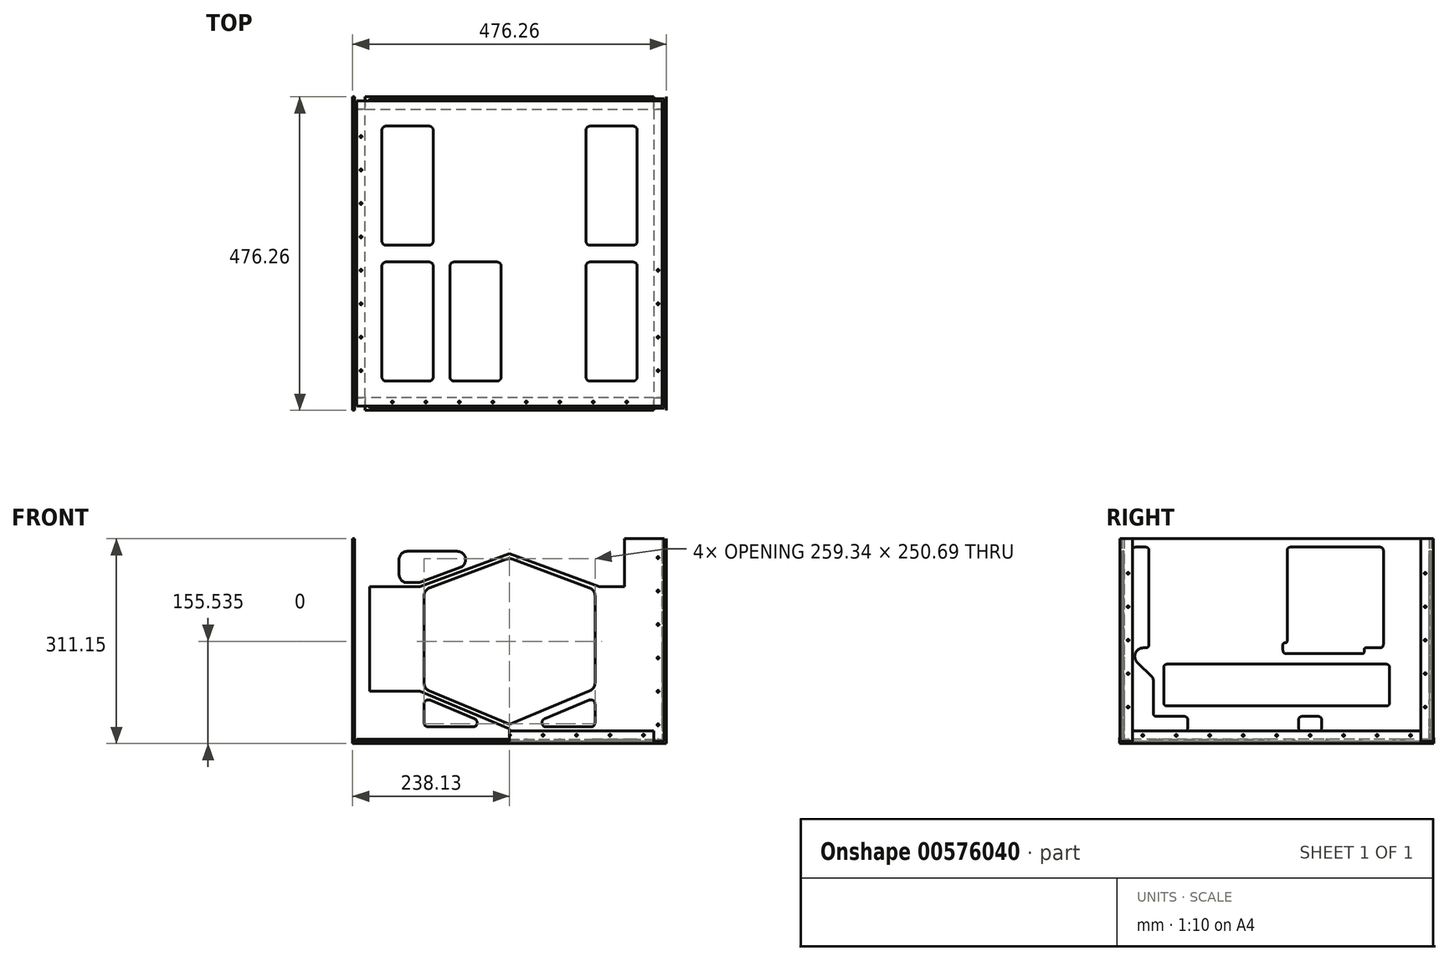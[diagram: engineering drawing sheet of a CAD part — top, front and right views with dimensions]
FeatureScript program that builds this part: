
annotation { "Feature Type Name" : "Feature", "Feature Type Description" : "" }
export const myFeature = defineFeature(function(context is Context, id is Id, definition is map)
    precondition{}
    {
        {
            var Q0;
            Q0=qCreatedBy(makeId("Top.planeOp"),FACE);
            var sketch = newSketch(context, id + "F0", { "sketchPlane" : qUnion([Q0])});
            skLineSegment(sketch, "E0.bottom", {"start": v(231.77, -231.77) * mm, "end": v(-231.78, -231.78) * mm});
            skLineSegment(sketch, "E0.top", {"start": v(231.77, 231.78) * mm, "end": v(-231.78, 231.77) * mm});
            skLineSegment(sketch, "E0.left", {"start": v(231.77, -231.77) * mm, "end": v(231.77, 231.78) * mm});
            skLineSegment(sketch, "E0.right", {"start": v(-231.78, -231.78) * mm, "end": v(-231.78, 231.77) * mm});
            skPoint(sketch, "E0.middle", {"position": v(0, 0) * mm});
            skLineSegment(sketch, "E1.0", {"start": v(234.95, -234.95) * mm, "end": v(234.95, 234.95) * mm});
            skLineSegment(sketch, "E1.1", {"start": v(234.95, -234.95) * mm, "end": v(-234.95, -234.95) * mm});
            skLineSegment(sketch, "E1.2", {"start": v(-234.95, -234.95) * mm, "end": v(-234.95, 234.95) * mm});
            skLineSegment(sketch, "E1.3", {"start": v(234.95, 234.95) * mm, "end": v(-234.95, 234.95) * mm});
            skLineSegment(sketch, "E2", {"start": v(-231.78, 231.77) * mm, "end": v(-234.95, 231.77) * mm});
            skLineSegment(sketch, "E3.MirrorCS", {"start": v(231.78, 231.77) * mm, "end": v(234.95, 231.77) * mm});
            skLineSegment(sketch, "E4.MirrorCS", {"start": v(-231.78, -231.77) * mm, "end": v(-234.95, -231.77) * mm});
            skLineSegment(sketch, "E5.MirrorCS", {"start": v(231.78, -231.77) * mm, "end": v(234.95, -231.77) * mm});
            skLineSegment(sketch, "E6.0", {"start": v(238.12, 238.13) * mm, "end": v(-238.13, 238.12) * mm});
            skLineSegment(sketch, "E6.1", {"start": v(238.12, -238.12) * mm, "end": v(238.12, 238.13) * mm});
            skLineSegment(sketch, "E6.2", {"start": v(238.12, -238.12) * mm, "end": v(-238.13, -238.13) * mm});
            skLineSegment(sketch, "E6.3", {"start": v(-238.13, -238.13) * mm, "end": v(-238.13, 238.12) * mm});
            skLineSegment(sketch, "E7", {"start": v(-238.13, 238.12) * mm, "end": v(-219.08, 238.12) * mm});
            skLineSegment(sketch, "E8", {"start": v(-219.08, 238.12) * mm, "end": v(-219.08, 234.95) * mm});
            skLineSegment(sketch, "E9", {"start": v(-238.13, 238.12) * mm, "end": v(-238.13, 219.07) * mm});
            skLineSegment(sketch, "E10", {"start": v(-238.13, 219.07) * mm, "end": v(-234.95, 219.07) * mm});
            skLineSegment(sketch, "E11.MirrorCS", {"start": v(238.13, 219.07) * mm, "end": v(234.95, 219.07) * mm});
            skLineSegment(sketch, "E12.MirrorCS", {"start": v(219.08, 238.12) * mm, "end": v(219.08, 234.95) * mm});
            skLineSegment(sketch, "E13.MirrorCS", {"start": v(238.13, 238.12) * mm, "end": v(219.08, 238.12) * mm});
            skLineSegment(sketch, "E14.MirrorCS", {"start": v(238.13, 238.12) * mm, "end": v(238.13, 219.07) * mm});
            skLineSegment(sketch, "E15.MirrorCS", {"start": v(-238.13, -219.07) * mm, "end": v(-234.95, -219.07) * mm});
            skLineSegment(sketch, "E16.MirrorCS", {"start": v(-219.08, -238.12) * mm, "end": v(-219.08, -234.95) * mm});
            skLineSegment(sketch, "E17.MirrorCS", {"start": v(-238.13, -238.12) * mm, "end": v(-238.13, -219.07) * mm});
            skLineSegment(sketch, "E18.MirrorCS", {"start": v(-238.13, -238.12) * mm, "end": v(-219.08, -238.12) * mm});
            skLineSegment(sketch, "E19.MirrorCS", {"start": v(238.13, -219.07) * mm, "end": v(234.95, -219.07) * mm});
            skLineSegment(sketch, "E20.MirrorCS", {"start": v(219.08, -238.12) * mm, "end": v(219.08, -234.95) * mm});
            skLineSegment(sketch, "E21.MirrorCS", {"start": v(238.13, -238.12) * mm, "end": v(219.08, -238.12) * mm});
            skLineSegment(sketch, "E22.MirrorCS", {"start": v(238.13, -238.12) * mm, "end": v(238.13, -219.07) * mm});
            skSolve(sketch);
        }
        {
            var Q0;
            Q0=makeQuery(id+"F0.imprint","IMPRINT",FACE,{"disambiguationData":[TD([[makeQuery(id+"F0.imprint","IMPRINT",EDGE,{"derivedFrom":sQuery(id+"F0.wireOp",EDGE,"E0.left")}),-1.0]])]});
            var Q1;
            Q1=makeQuery(id+"F0.imprint","IMPRINT",FACE,{"disambiguationData":[TD([[makeQuery(id+"F0.imprint","IMPRINT",EDGE,{"derivedFrom":sQuery(id+"F0.wireOp",EDGE,"E0.right")}),1.0]])]});
            extrude(context, id + "F1", {"entities" : qUnion([Q0, Q1]), "depth" : 307.97 * mm, "offsetDistance" : 25.4 * mm});
        }
        {
            var Q0;
            Q0=makeQuery(id+"F0.imprint","IMPRINT",FACE,{"disambiguationData":[TD([[makeQuery(id+"F0.imprint","IMPRINT",EDGE,{"derivedFrom":sQuery(id+"F0.wireOp",EDGE,"E0.top")}),-1.0]])]});
            var Q1;
            Q1=makeQuery(id+"F0.imprint","IMPRINT",FACE,{"disambiguationData":[TD([[makeQuery(id+"F0.imprint","IMPRINT",EDGE,{"derivedFrom":sQuery(id+"F0.wireOp",EDGE,"E0.bottom")}),1.0]])]});
            extrude(context, id + "F2", {"entities" : qUnion([Q0, Q1]), "depth" : 307.97 * mm, "offsetDistance" : 25.4 * mm});
        }
        {
            var Q0;
            {var subQ0=sQuery(id+"F0.wireOp",EDGE,"E15.MirrorCS");Q0=makeQuery(id+"F0.imprint","IMPRINT",FACE,{"disambiguationData":[TD([[makeQuery(id+"F0.imprint","IMPRINT",EDGE,{"derivedFrom":subQ0}),-1.0]])]});}
            var Q1;
            {var subQ0=sQuery(id+"F0.wireOp",EDGE,"E19.MirrorCS");Q1=makeQuery(id+"F0.imprint","IMPRINT",FACE,{"disambiguationData":[TD([[makeQuery(id+"F0.imprint","IMPRINT",EDGE,{"derivedFrom":subQ0}),1.0]])]});}
            var Q2;
            {var subQ0=sQuery(id+"F0.wireOp",EDGE,"E11.MirrorCS");Q2=makeQuery(id+"F0.imprint","IMPRINT",FACE,{"disambiguationData":[TD([[makeQuery(id+"F0.imprint","IMPRINT",EDGE,{"derivedFrom":subQ0}),-1.0]])]});}
            var Q3;
            Q3=makeQuery(id+"F0.imprint","IMPRINT",FACE,{"disambiguationData":[TD([[makeQuery(id+"F0.imprint","IMPRINT",EDGE,{"derivedFrom":sQuery(id+"F0.wireOp",EDGE,"E7")}),-1.0]])]});
            extrude(context, id + "F3", {"entities" : qUnion([Q0, Q1, Q2, Q3]), "depth" : 307.97 * mm, "offsetDistance" : 25.4 * mm});
        }
        {
            var Q0;
            Q0=makeQuery(id+"F3.opExtrude","SWEPT_FACE",FACE,{"disambiguationData":[OSD([sQuery(id+"F0.wireOp",EDGE,"E16.MirrorCS")])]});
            var sketch = newSketch(context, id + "F4", { "sketchPlane" : qUnion([Q0])});
            skLineSegment(sketch, "E23", {"start": v(-234.95, 0) * mm, "end": v(-234.95, -3.18) * mm});
            skLineSegment(sketch, "E24", {"start": v(-234.95, -3.18) * mm, "end": v(-238.13, -3.18) * mm});
            skLineSegment(sketch, "E25", {"start": v(-238.13, -3.18) * mm, "end": v(-238.12, 15.88) * mm});
            skLineSegment(sketch, "E26", {"start": v(-238.12, 15.88) * mm, "end": v(-234.95, 15.88) * mm});
            skLineSegment(sketch, "E27", {"start": v(-234.95, 15.88) * mm, "end": v(-234.95, 0) * mm});
            skLineSegment(sketch, "E28", {"start": v(-238.13, -3.18) * mm, "end": v(-219.08, -3.18) * mm});
            skLineSegment(sketch, "E29", {"start": v(-219.08, -3.18) * mm, "end": v(-219.08, 0) * mm});
            skLineSegment(sketch, "E30", {"start": v(-219.08, 0) * mm, "end": v(-234.95, 0) * mm});
            skSolve(sketch);
        }
        {
            var Q0;
            Q0=qSketchRegion(id+"F4",true);
            extrude(context, id + "F5", {"entities" : qUnion([Q0]), "depth" : 438.15 * mm, "offsetDistance" : 25.4 * mm});
        }
        {
            var Q0;
            Q0=qCreatedBy(makeId("Front.planeOp"),FACE);
            var sketch = newSketch(context, id + "F6", { "sketchPlane" : qUnion([Q0])});
            skLineSegment(sketch, "E31", {"start": v(0, 0) * mm, "end": v(0, 52.73) * mm});
            skSolve(sketch);
        }
        {
            var Q0;
            Q0=makeQuery(id+"F5.opExtrude","SWEPT_BODY",BODY,{"disambiguationData":[OSD([sQuery(id+"F4.wireOp",EDGE,"E25"),sQuery(id+"F4.wireOp",EDGE,"E26"),sQuery(id+"F4.wireOp",EDGE,"E27"),sQuery(id+"F4.wireOp",EDGE,"E28"),sQuery(id+"F4.wireOp",EDGE,"E29"),sQuery(id+"F4.wireOp",EDGE,"E30")])]});
            var Q1;
            Q1=sQuery(id+"F6.wireOp",EDGE,"E31");
            circularPattern(context, id + "F7", {"entities" : qUnion([Q0]), "axis" : qUnion([Q1]), "angle" : 360 * degree, "instanceCount" : 4, "equalSpace" : true});
        }
        {
            var Q0;
            Q0=makeQuery(id+"F2.opExtrude","SWEPT_FACE",FACE,{"disambiguationData":[OSD([sQuery(id+"F0.wireOp",EDGE,"E1.1")])]});
            var sketch = newSketch(context, id + "F8", { "sketchPlane" : qUnion([Q0])});
            skLineSegment(sketch, "E32.bottom", {"start": v(212.22, 76.2) * mm, "end": v(136.02, 76.2) * mm});
            skLineSegment(sketch, "E32.top", {"start": v(212.22, 234.95) * mm, "end": v(136.02, 234.95) * mm});
            skLineSegment(sketch, "E32.left", {"start": v(212.22, 76.2) * mm, "end": v(212.22, 234.95) * mm});
            skLineSegment(sketch, "E32.right", {"start": v(136.02, 76.2) * mm, "end": v(136.02, 234.95) * mm});
            skPoint(sketch, "E32.middle", {"position": v(174.12, 155.58) * mm});
            skLineSegment(sketch, "E33", {"start": v(219.08, 307.98) * mm, "end": v(174.12, 307.98) * mm});
            skLineSegment(sketch, "E34", {"start": v(174.12, 307.98) * mm, "end": v(174.12, 155.58) * mm});
            skLineSegment(sketch, "E35", {"start": v(0, 307.98) * mm, "end": v(0, 348.73) * mm});
            skPoint(sketch, "E35.endSnap0", {"position": v(0, 307.98) * mm});
            skLineSegment(sketch, "E36", {"start": v(219.08, 307.98) * mm, "end": v(219.08, 288.93) * mm});
            skLineSegment(sketch, "E37", {"start": v(206.38, 288.93) * mm, "end": v(193.17, 288.93) * mm});
            skLineSegment(sketch, "E38", {"start": v(136.02, 234.95) * mm, "end": v(-2.34, 286.18) * mm});
            skLineSegment(sketch, "E39", {"start": v(136.02, 76.2) * mm, "end": v(0, 19.05) * mm});
            skLineSegment(sketch, "E40.0", {"start": v(135.02, 242.1) * mm, "end": v(75, 264.32) * mm});
            skLineSegment(sketch, "E41.0", {"start": v(121.38, 233.6) * mm, "end": v(4.4, 276.9) * mm});
            skLineSegment(sketch, "E42.0", {"start": v(121.89, 77.15) * mm, "end": v(4.92, 28) * mm});
            skLineSegment(sketch, "E43.0", {"start": v(167.77, 276.23) * mm, "end": v(167.77, 254) * mm});
            skLineSegment(sketch, "E44.0", {"start": v(180.47, 276.23) * mm, "end": v(180.47, 254) * mm});
            skLineSegment(sketch, "E45", {"start": v(212.22, 234.95) * mm, "end": v(219.07, 234.95) * mm});
            skLineSegment(sketch, "E46", {"start": v(212.22, 76.2) * mm, "end": v(219.07, 76.2) * mm});
            skLineSegment(sketch, "E47.1", {"start": v(212.22, 241.3) * mm, "end": v(219.07, 241.3) * mm});
            skLineSegment(sketch, "E47.2", {"start": v(155.07, 241.3) * mm, "end": v(139.43, 241.3) * mm});
            skLineSegment(sketch, "E47.3", {"start": v(129.67, 88.86) * mm, "end": v(129.67, 221.69) * mm});
            skLineSegment(sketch, "E48", {"start": v(0, -253.23) * mm, "end": v(0, 278.54) * mm});
            skArc(sketch, "E49.filletArc", {"start": v(129.67, 221.69) * mm, "mid": v(127.4, 228.95) * mm, "end": v(121.38, 233.6) * mm});
            skArc(sketch, "E50.filletArc", {"start": v(121.89, 77.15) * mm, "mid": v(127.54, 81.83) * mm, "end": v(129.67, 88.86) * mm});
            skArc(sketch, "E51.filletArc", {"start": v(135.02, 242.1) * mm, "mid": v(137.2, 241.5) * mm, "end": v(139.43, 241.3) * mm});
            skArc(sketch, "E52.filletArc", {"start": v(155.07, 241.3) * mm, "mid": v(164.05, 245.02) * mm, "end": v(167.77, 254) * mm});
            skLineSegment(sketch, "E53", {"start": v(206.37, 241.3) * mm, "end": v(193.17, 241.3) * mm});
            skArc(sketch, "E54.filletArc", {"start": v(180.47, 254) * mm, "mid": v(184.19, 245.02) * mm, "end": v(193.17, 241.3) * mm});
            skLineSegment(sketch, "E55", {"start": v(219.08, 276.23) * mm, "end": v(219.08, 254) * mm});
            skPoint(sketch, "E56.visualSharp", {"position": v(219.07, 241.3) * mm});
            skArc(sketch, "E56.filletArc", {"start": v(206.37, 241.3) * mm, "mid": v(215.36, 245.02) * mm, "end": v(219.07, 254) * mm});
            skPoint(sketch, "E57.visualSharp", {"position": v(219.08, 288.93) * mm});
            skArc(sketch, "E57.filletArc", {"start": v(219.08, 276.23) * mm, "mid": v(215.36, 285.2) * mm, "end": v(206.38, 288.93) * mm});
            skPoint(sketch, "E58.newPointB", {"position": v(0, 288.93) * mm});
            skArc(sketch, "E58.filletArc", {"start": v(193.17, 288.93) * mm, "mid": v(184.19, 285.2) * mm, "end": v(180.47, 276.23) * mm});
            skPoint(sketch, "E59.visualSharp", {"position": v(219.08, 15.88) * mm});
            skPoint(sketch, "E60.newPointB", {"position": v(0, 15.87) * mm});
            skLineSegment(sketch, "E61", {"start": v(155.07, 288.93) * mm, "end": v(79.4, 288.93) * mm});
            skArc(sketch, "E62.filletArc", {"start": v(167.77, 276.23) * mm, "mid": v(164.05, 285.2) * mm, "end": v(155.07, 288.93) * mm});
            skPoint(sketch, "E63.visualSharp", {"position": v(8.53, 288.93) * mm});
            skArc(sketch, "E63.filletArc", {"start": v(79.4, 288.93) * mm, "mid": v(66.9, 278.46) * mm, "end": v(75, 264.32) * mm});
            skPoint(sketch, "E64.visualSharp", {"position": v(8.76, 15.88) * mm});
            skPoint(sketch, "E65.visualSharp", {"position": v(167.77, 15.88) * mm});
            skArc(sketch, "E66.MirrorCS", {"start": v(-135.02, 242.1) * mm, "mid": v(-137.2, 241.5) * mm, "end": v(-139.43, 241.3) * mm});
            skLineSegment(sketch, "E67.MirrorCS", {"start": v(-212.22, 241.3) * mm, "end": v(-219.07, 241.3) * mm});
            skLineSegment(sketch, "E68.MirrorCS", {"start": v(-212.22, 234.95) * mm, "end": v(-219.07, 234.95) * mm});
            skLineSegment(sketch, "E69.MirrorCS", {"start": v(-136.02, 76.2) * mm, "end": v(0, 19.05) * mm});
            skArc(sketch, "E70.MirrorCS", {"start": v(-167.77, 276.23) * mm, "mid": v(-164.05, 285.2) * mm, "end": v(-155.07, 288.93) * mm});
            skLineSegment(sketch, "E71.MirrorCS", {"start": v(-136.02, 234.95) * mm, "end": v(2.34, 286.18) * mm});
            skArc(sketch, "E72.MirrorCS", {"start": v(-219.07, 276.23) * mm, "mid": v(-215.36, 285.2) * mm, "end": v(-206.37, 288.93) * mm});
            skLineSegment(sketch, "E73.MirrorCS", {"start": v(-219.07, 307.98) * mm, "end": v(-219.07, 288.93) * mm});
            skLineSegment(sketch, "E74.MirrorCS", {"start": v(-129.67, 88.86) * mm, "end": v(-129.67, 221.69) * mm});
            skLineSegment(sketch, "E75.MirrorCS", {"start": v(-206.37, 288.92) * mm, "end": v(-193.17, 288.92) * mm});
            skLineSegment(sketch, "E76.MirrorCS", {"start": v(-174.12, 307.98) * mm, "end": v(-174.12, 155.57) * mm});
            skLineSegment(sketch, "E77.MirrorCS", {"start": v(-121.89, 77.15) * mm, "end": v(-4.92, 28) * mm});
            skPoint(sketch, "E78.MirrorP", {"position": v(-219.07, 288.93) * mm});
            skPoint(sketch, "E79.MirrorP", {"position": v(-174.12, 155.57) * mm});
            skPoint(sketch, "E80.MirrorP", {"position": v(-8.53, 288.93) * mm});
            skLineSegment(sketch, "E81.MirrorCS", {"start": v(-136.02, 76.2) * mm, "end": v(-136.02, 234.95) * mm});
            skLineSegment(sketch, "E82.MirrorCS", {"start": v(-212.22, 76.2) * mm, "end": v(-212.22, 234.95) * mm});
            skLineSegment(sketch, "E83.MirrorCS", {"start": v(-219.07, 307.98) * mm, "end": v(-174.12, 307.98) * mm});
            skLineSegment(sketch, "E84.MirrorCS", {"start": v(-212.22, 234.95) * mm, "end": v(-136.02, 234.95) * mm});
            skLineSegment(sketch, "E85.MirrorCS", {"start": v(-155.07, 241.3) * mm, "end": v(-139.43, 241.3) * mm});
            skArc(sketch, "E86.MirrorCS", {"start": v(-79.4, 288.93) * mm, "mid": v(-66.9, 278.46) * mm, "end": v(-75, 264.32) * mm});
            skPoint(sketch, "E87.MirrorP", {"position": v(-219.07, 241.3) * mm});
            skLineSegment(sketch, "E88.MirrorCS", {"start": v(-206.37, 241.3) * mm, "end": v(-193.17, 241.3) * mm});
            skPoint(sketch, "E89.MirrorP", {"position": v(-8.76, 15.88) * mm});
            skLineSegment(sketch, "E90.MirrorCS", {"start": v(-155.07, 288.93) * mm, "end": v(-79.4, 288.93) * mm});
            skArc(sketch, "E91.MirrorCS", {"start": v(-193.17, 288.93) * mm, "mid": v(-184.19, 285.2) * mm, "end": v(-180.47, 276.23) * mm});
            skLineSegment(sketch, "E92.MirrorCS", {"start": v(-180.47, 276.23) * mm, "end": v(-180.47, 254) * mm});
            skLineSegment(sketch, "E93.MirrorCS", {"start": v(-219.07, 276.23) * mm, "end": v(-219.07, 254) * mm});
            skArc(sketch, "E94.MirrorCS", {"start": v(-121.89, 77.15) * mm, "mid": v(-127.54, 81.83) * mm, "end": v(-129.67, 88.86) * mm});
            skLineSegment(sketch, "E95.MirrorCS", {"start": v(-167.77, 276.23) * mm, "end": v(-167.77, 254) * mm});
            skArc(sketch, "E96.MirrorCS", {"start": v(-206.37, 241.3) * mm, "mid": v(-215.36, 245.02) * mm, "end": v(-219.07, 254) * mm});
            skLineSegment(sketch, "E97.MirrorCS", {"start": v(-135.02, 242.1) * mm, "end": v(-75, 264.32) * mm});
            skArc(sketch, "E98.MirrorCS", {"start": v(-129.67, 221.69) * mm, "mid": v(-127.4, 228.95) * mm, "end": v(-121.38, 233.6) * mm});
            skArc(sketch, "E99.MirrorCS", {"start": v(-155.07, 241.3) * mm, "mid": v(-164.05, 245.02) * mm, "end": v(-167.77, 254) * mm});
            skArc(sketch, "E100.MirrorCS", {"start": v(-180.47, 254) * mm, "mid": v(-184.19, 245.02) * mm, "end": v(-193.17, 241.3) * mm});
            skLineSegment(sketch, "E101.MirrorCS", {"start": v(-121.38, 233.6) * mm, "end": v(-4.4, 276.9) * mm});
            skLineSegment(sketch, "E102.trimOffspring", {"start": v(0, 19.82) * mm, "end": v(0, 25.94) * mm});
            skPoint(sketch, "E103.visualSharp", {"position": v(0, 278.54) * mm});
            skArc(sketch, "E103.filletArc", {"start": v(4.4, 276.9) * mm, "mid": v(0, 277.7) * mm, "end": v(-4.4, 276.9) * mm});
            skPoint(sketch, "E104.visualSharp", {"position": v(0, 25.94) * mm});
            skArc(sketch, "E104.filletArc", {"start": v(-4.92, 28) * mm, "mid": v(0, 27.01) * mm, "end": v(4.92, 28) * mm});
            skLineSegment(sketch, "E105", {"start": v(136.02, 76.2) * mm, "end": v(136.02, 15.87) * mm});
            skPoint(sketch, "E106.orphan", {"position": v(136.02, 47.68) * mm});
            skPoint(sketch, "E64.filletArc.start.orphan", {"position": v(75.56, 22.28) * mm});
            skPoint(sketch, "E107.0.start.orphan", {"position": v(180.47, 53.98) * mm});
            skPoint(sketch, "E108.end.orphan", {"position": v(174.12, 15.88) * mm});
            skPoint(sketch, "E108.start.orphan", {"position": v(174.12, 76.2) * mm});
            skPoint(sketch, "E109.end.orphan", {"position": v(193.17, 66.68) * mm});
            skPoint(sketch, "E110.filletArc.end.orphan", {"position": v(206.38, 66.68) * mm});
            skPoint(sketch, "E60.filletArc.start.orphan", {"position": v(180.47, 28.58) * mm});
            skPoint(sketch, "E111.0.end.orphan", {"position": v(167.77, 28.58) * mm});
            skPoint(sketch, "E111.0.start.orphan", {"position": v(167.77, 57.15) * mm});
            skPoint(sketch, "E47.4.end.orphan", {"position": v(139.86, 69.85) * mm});
            skPoint(sketch, "E47.4.start.orphan", {"position": v(155.07, 69.85) * mm});
            skPoint(sketch, "E47.0.end.orphan", {"position": v(219.08, 69.85) * mm});
            skPoint(sketch, "E47.0.start.orphan", {"position": v(212.22, 69.85) * mm});
            skPoint(sketch, "E112.end.orphan", {"position": v(155.07, 15.88) * mm});
            skPoint(sketch, "E113.end.orphan", {"position": v(219.08, 28.58) * mm});
            skPoint(sketch, "E113.start.orphan", {"position": v(219.08, 53.98) * mm});
            skPoint(sketch, "E114.end.orphan", {"position": v(193.17, 15.88) * mm});
            skPoint(sketch, "E114.start.orphan", {"position": v(206.38, 15.88) * mm});
            skLineSegment(sketch, "E115", {"start": v(136.02, 15.87) * mm, "end": v(0, 15.87) * mm});
            skLineSegment(sketch, "E116.0", {"start": v(123.32, 22.22) * mm, "end": v(55.46, 22.22) * mm});
            skLineSegment(sketch, "E117.0", {"start": v(120.86, 62.94) * mm, "end": v(53, 34.43) * mm});
            skLineSegment(sketch, "E118.trimOffspring", {"start": v(129.67, 57.09) * mm, "end": v(129.67, 28.57) * mm});
            skPoint(sketch, "E119.visualSharp", {"position": v(23.95, 22.22) * mm});
            skArc(sketch, "E119.filletArc", {"start": v(53, 34.43) * mm, "mid": v(49.23, 27.32) * mm, "end": v(55.46, 22.22) * mm});
            skPoint(sketch, "E120.visualSharp", {"position": v(129.67, 22.22) * mm});
            skArc(sketch, "E120.filletArc", {"start": v(123.32, 22.22) * mm, "mid": v(127.8, 24.08) * mm, "end": v(129.67, 28.57) * mm});
            skPoint(sketch, "E121.visualSharp", {"position": v(129.67, 66.64) * mm});
            skArc(sketch, "E121.filletArc", {"start": v(129.67, 57.09) * mm, "mid": v(126.83, 62.38) * mm, "end": v(120.86, 62.94) * mm});
            skArc(sketch, "E122.MirrorCS", {"start": v(-53, 34.43) * mm, "mid": v(-49.23, 27.32) * mm, "end": v(-55.46, 22.22) * mm});
            skLineSegment(sketch, "E123.MirrorCS", {"start": v(-120.86, 62.94) * mm, "end": v(-53, 34.43) * mm});
            skArc(sketch, "E124.MirrorCS", {"start": v(-129.67, 57.09) * mm, "mid": v(-126.83, 62.38) * mm, "end": v(-120.86, 62.94) * mm});
            skLineSegment(sketch, "E125.MirrorCS", {"start": v(-129.67, 57.09) * mm, "end": v(-129.67, 28.57) * mm});
            skArc(sketch, "E126.MirrorCS", {"start": v(-123.32, 22.22) * mm, "mid": v(-127.8, 24.08) * mm, "end": v(-129.67, 28.57) * mm});
            skLineSegment(sketch, "E127.MirrorCS", {"start": v(-123.32, 22.22) * mm, "end": v(-55.46, 22.22) * mm});
            skLineSegment(sketch, "E128.MirrorCS", {"start": v(-212.22, 76.2) * mm, "end": v(-136.02, 76.2) * mm});
            skLineSegment(sketch, "E129.MirrorCS", {"start": v(-136.02, 76.2) * mm, "end": v(-136.02, 15.87) * mm});
            skSolve(sketch);
        }
        {
            var Q0;
            Q0=makeQuery(id+"F8.imprint","IMPRINT",FACE,{"disambiguationData":[TD([[makeQuery(id+"F8.imprint","IMPRINT",EDGE,{"derivedFrom":sQuery(id+"F8.wireOp",EDGE,"E37")}),1.0]])]});
            var Q1;
            Q1=makeQuery(id+"F8.imprint","IMPRINT",FACE,{"disambiguationData":[TD([[makeQuery(id+"F8.imprint","IMPRINT",EDGE,{"derivedFrom":sQuery(id+"F8.wireOp",EDGE,"E40.0")}),-1.0]])]});
            var Q2;
            Q2=makeQuery(id+"F8.imprint","IMPRINT",FACE,{"disambiguationData":[TD([[makeQuery(id+"F8.imprint","IMPRINT",EDGE,{"derivedFrom":sQuery(id+"F8.wireOp",EDGE,"E66.MirrorCS")}),-1.0]])]});
            var Q3;
            Q3=makeQuery(id+"F8.imprint","IMPRINT",FACE,{"disambiguationData":[TD([[makeQuery(id+"F8.imprint","IMPRINT",EDGE,{"derivedFrom":sQuery(id+"F8.wireOp",EDGE,"E72.MirrorCS")}),-1.0]])]});
            var Q4;
            Q4=makeQuery(id+"F8.imprint","IMPRINT",FACE,{"disambiguationData":[TD([[makeQuery(id+"F8.imprint","IMPRINT",EDGE,{"derivedFrom":sQuery(id+"F8.wireOp",EDGE,"E41.0")}),1.0]])]});
            var Q5;
            Q5=makeQuery(id+"F8.imprint","IMPRINT",FACE,{"disambiguationData":[TD([[makeQuery(id+"F8.imprint","IMPRINT",EDGE,{"derivedFrom":sQuery(id+"F8.wireOp",EDGE,"E74.MirrorCS")}),-1.0]])]});
            var Q6;
            Q6=makeQuery(id+"F8.imprint","IMPRINT",FACE,{"disambiguationData":[TD([[makeQuery(id+"F8.imprint","IMPRINT",EDGE,{"derivedFrom":sQuery(id+"F8.wireOp",EDGE,"E122.MirrorCS")}),-1.0]])]});
            var Q7;
            Q7=makeQuery(id+"F8.imprint","IMPRINT",FACE,{"disambiguationData":[TD([[makeQuery(id+"F8.imprint","IMPRINT",EDGE,{"derivedFrom":sQuery(id+"F8.wireOp",EDGE,"E116.0")}),-1.0]])]});
            extrude(context, id + "F9", {"entities" : qUnion([Q0, Q1, Q2, Q3, Q4, Q5, Q6, Q7]), "operationType" : NewBodyOperationType.REMOVE, "endBound" : BoundingType.SYMMETRIC, "oppositeDirection" : true, "depth" : 2540 * mm, "offsetDistance" : 25.4 * mm});
        }
        {
            var Q0;
            Q0=makeQuery(id+"F1.opExtrude","SWEPT_FACE",FACE,{"disambiguationData":[OSD([sQuery(id+"F0.wireOp",EDGE,"E1.0")])]});
            var sketch = newSketch(context, id + "F10", { "sketchPlane" : qUnion([Q0])});
            skLineSegment(sketch, "E130.bottom", {"start": v(9.53, 156.24) * mm, "end": v(-9.53, 156.24) * mm});
            skLineSegment(sketch, "E130.top", {"start": v(9.53, 307.98) * mm, "end": v(-9.53, 307.98) * mm});
            skLineSegment(sketch, "E130.left", {"start": v(9.53, 156.24) * mm, "end": v(9.52, 307.98) * mm});
            skLineSegment(sketch, "E130.right", {"start": v(-9.53, 156.24) * mm, "end": v(-9.52, 307.98) * mm});
            skPoint(sketch, "E130.middle", {"position": v(0, 232.1) * mm});
            skLineSegment(sketch, "E131.bottom", {"start": v(180.98, 44.45) * mm, "end": v(128.59, 44.45) * mm});
            skLineSegment(sketch, "E131.top", {"start": v(139.06, 127) * mm, "end": v(-139.07, 127) * mm});
            skLineSegment(sketch, "E131.left", {"start": v(180.98, 44.45) * mm, "end": v(180.98, 127) * mm});
            skLineSegment(sketch, "E131.right", {"start": v(-180.97, 44.45) * mm, "end": v(-180.97, 98.97) * mm});
            skPoint(sketch, "E131.middle", {"position": v(0, 85.73) * mm});
            skLineSegment(sketch, "E132", {"start": v(0, 85.73) * mm, "end": v(0, 15.88) * mm});
            skLineSegment(sketch, "E133", {"start": v(-26.99, 15.88) * mm, "end": v(-219.08, 15.88) * mm});
            skLineSegment(sketch, "E134", {"start": v(0, 307.98) * mm, "end": v(0, 335.86) * mm});
            skLineSegment(sketch, "E135", {"start": v(0, 307.98) * mm, "end": v(-88.9, 307.98) * mm});
            skLineSegment(sketch, "E136", {"start": v(-88.9, 307.98) * mm, "end": v(-88.9, 343.75) * mm});
            skArc(sketch, "E137", {"start": v(-202.56, 135.9) * mm, "mid": v(-208.43, 131.97) * mm, "end": v(-207.06, 125.05) * mm});
            skLineSegment(sketch, "E138", {"start": v(-202.56, 129.54) * mm, "end": v(-202.56, 123.2) * mm});
            skLineSegment(sketch, "E139", {"start": v(-202.56, 15.88) * mm, "end": v(-219.08, 15.88) * mm});
            skLineSegment(sketch, "E140.left", {"start": v(26.99, 25.4) * mm, "end": v(26.99, 44.45) * mm});
            skLineSegment(sketch, "E140.right", {"start": v(-26.99, 25.4) * mm, "end": v(-26.99, 44.45) * mm});
            skPoint(sketch, "E140.middle", {"position": v(0, 34.92) * mm});
            skLineSegment(sketch, "E141", {"start": v(0, 34.92) * mm, "end": v(0, 44.45) * mm});
            skLineSegment(sketch, "E142", {"start": v(0, 44.45) * mm, "end": v(0, 85.73) * mm});
            skLineSegment(sketch, "E143", {"start": v(-26.99, 44.45) * mm, "end": v(-50.8, 44.45) * mm});
            skLineSegment(sketch, "E144", {"start": v(-50.8, 44.45) * mm, "end": v(-50.8, 71.82) * mm});
            skLineSegment(sketch, "E145", {"start": v(-26.99, 25.4) * mm, "end": v(-26.99, 15.88) * mm});
            skLineSegment(sketch, "E146", {"start": v(26.99, 25.4) * mm, "end": v(26.99, 15.88) * mm});
            skLineSegment(sketch, "E147.MirrorCS", {"start": v(-187.33, 307.98) * mm, "end": v(-168.28, 307.98) * mm});
            skPoint(sketch, "E148.MirrorP", {"position": v(-177.8, 232.1) * mm});
            skLineSegment(sketch, "E149.MirrorCS", {"start": v(-187.33, 156.24) * mm, "end": v(-168.28, 156.24) * mm});
            skLineSegment(sketch, "E150.MirrorCS", {"start": v(-177.8, 307.98) * mm, "end": v(-88.9, 307.98) * mm});
            skLineSegment(sketch, "E151.MirrorCS", {"start": v(-168.27, 156.24) * mm, "end": v(-168.28, 307.98) * mm});
            skLineSegment(sketch, "E152.MirrorCS", {"start": v(-177.8, 307.98) * mm, "end": v(-177.8, 335.86) * mm});
            skLineSegment(sketch, "E153.MirrorCS", {"start": v(-187.33, 156.24) * mm, "end": v(-187.33, 307.98) * mm});
            skLineSegment(sketch, "E154.MirrorCS", {"start": v(187.33, 307.98) * mm, "end": v(168.28, 307.98) * mm});
            skLineSegment(sketch, "E155.MirrorCS", {"start": v(177.8, 307.98) * mm, "end": v(177.8, 335.86) * mm});
            skLineSegment(sketch, "E156.MirrorCS", {"start": v(177.8, 307.98) * mm, "end": v(88.9, 307.98) * mm});
            skLineSegment(sketch, "E157.MirrorCS", {"start": v(168.27, 156.24) * mm, "end": v(168.28, 307.98) * mm});
            skPoint(sketch, "E158.MirrorP", {"position": v(177.8, 232.1) * mm});
            skLineSegment(sketch, "E159.MirrorCS", {"start": v(187.33, 156.24) * mm, "end": v(187.33, 307.98) * mm});
            skLineSegment(sketch, "E160.MirrorCS", {"start": v(88.9, 307.98) * mm, "end": v(88.9, 343.75) * mm});
            skLineSegment(sketch, "E161.MirrorCS", {"start": v(187.33, 156.24) * mm, "end": v(168.28, 156.24) * mm});
            skLineSegment(sketch, "E162.MirrorCS", {"start": v(0, 307.98) * mm, "end": v(88.9, 307.98) * mm});
            skLineSegment(sketch, "E163.MirrorCS", {"start": v(-101.6, 34.92) * mm, "end": v(-101.6, 44.45) * mm});
            skLineSegment(sketch, "E164.MirrorCS", {"start": v(-74.61, 25.4) * mm, "end": v(-74.61, 15.88) * mm});
            skLineSegment(sketch, "E165.MirrorCS", {"start": v(-128.59, 25.4) * mm, "end": v(-128.59, 15.88) * mm});
            skLineSegment(sketch, "E166.MirrorCS", {"start": v(-128.59, 25.4) * mm, "end": v(-128.59, 44.45) * mm});
            skLineSegment(sketch, "E167.MirrorCS", {"start": v(-74.61, 44.45) * mm, "end": v(-50.8, 44.45) * mm});
            skPoint(sketch, "E168.MirrorP", {"position": v(-101.6, 34.92) * mm});
            skLineSegment(sketch, "E169.MirrorCS", {"start": v(-74.61, 25.4) * mm, "end": v(-74.61, 44.45) * mm});
            skLineSegment(sketch, "E170.MirrorCS", {"start": v(101.6, 34.92) * mm, "end": v(101.6, 44.45) * mm});
            skLineSegment(sketch, "E171.MirrorCS", {"start": v(128.59, 25.4) * mm, "end": v(128.59, 15.88) * mm});
            skLineSegment(sketch, "E172.MirrorCS", {"start": v(74.61, 25.4) * mm, "end": v(74.61, 15.88) * mm});
            skLineSegment(sketch, "E173.MirrorCS", {"start": v(-26.99, 25.4) * mm, "end": v(-26.99, 15.87) * mm});
            skLineSegment(sketch, "E174.MirrorCS", {"start": v(74.61, 44.45) * mm, "end": v(50.8, 44.45) * mm});
            skLineSegment(sketch, "E175.MirrorCS", {"start": v(128.59, 25.4) * mm, "end": v(128.59, 44.45) * mm});
            skLineSegment(sketch, "E176.MirrorCS", {"start": v(74.61, 25.4) * mm, "end": v(74.61, 44.45) * mm});
            skLineSegment(sketch, "E177.MirrorCS", {"start": v(26.99, 44.45) * mm, "end": v(50.8, 44.45) * mm});
            skLineSegment(sketch, "E178.MirrorCS", {"start": v(50.8, 44.45) * mm, "end": v(50.8, 71.82) * mm});
            skPoint(sketch, "E179.MirrorP", {"position": v(101.6, 34.92) * mm});
            skArc(sketch, "E180.MirrorC", {"start": v(202.56, 135.9) * mm, "mid": v(208.43, 131.97) * mm, "end": v(207.06, 125.05) * mm});
            skLineSegment(sketch, "E181", {"start": v(-219.07, 290.2) * mm, "end": v(-219.07, 20.96) * mm});
            skLineSegment(sketch, "E182.MirrorCS", {"start": v(219.07, 290.2) * mm, "end": v(219.07, 20.96) * mm});
            skLineSegment(sketch, "E183", {"start": v(-219.07, 307.98) * mm, "end": v(219.07, 307.98) * mm});
            skLineSegment(sketch, "E184", {"start": v(-214, 15.88) * mm, "end": v(-140.02, 15.88) * mm});
            skLineSegment(sketch, "E185", {"start": v(-219.07, 307.98) * mm, "end": v(-219.07, 295.28) * mm});
            skLineSegment(sketch, "E186", {"start": v(-156.85, 293.69) * mm, "end": v(-20.96, 293.69) * mm});
            skLineSegment(sketch, "E187.0", {"start": v(-15.88, 152.43) * mm, "end": v(-15.88, 288.6) * mm});
            skLineSegment(sketch, "E187.1", {"start": v(13.34, 149.89) * mm, "end": v(12.07, 149.89) * mm});
            skLineSegment(sketch, "E187.2", {"start": v(15.88, 152.43) * mm, "end": v(15.88, 290.2) * mm});
            skLineSegment(sketch, "E188.0", {"start": v(-193.67, 149.89) * mm, "end": v(-193.67, 290.2) * mm});
            skLineSegment(sketch, "E188.2", {"start": v(-161.93, 149.89) * mm, "end": v(-161.93, 288.6) * mm});
            skLineSegment(sketch, "E189.0", {"start": v(161.93, 149.89) * mm, "end": v(161.93, 290.2) * mm});
            skLineSegment(sketch, "E189.2", {"start": v(193.67, 149.89) * mm, "end": v(193.67, 290.2) * mm});
            skLineSegment(sketch, "E190", {"start": v(-202.56, 135.9) * mm, "end": v(-139.07, 135.9) * mm});
            skLineSegment(sketch, "E191", {"start": v(-139.07, 135.9) * mm, "end": v(-139.07, 127) * mm});
            skLineSegment(sketch, "E192", {"start": v(-202.57, 129.54) * mm, "end": v(-207.06, 125.05) * mm});
            skLineSegment(sketch, "E193", {"start": v(-207.06, 125.05) * mm, "end": v(-180.97, 98.97) * mm});
            skLineSegment(sketch, "E194.MirrorCS", {"start": v(202.57, 129.54) * mm, "end": v(207.06, 125.05) * mm});
            skLineSegment(sketch, "E195.MirrorCS", {"start": v(202.56, 129.54) * mm, "end": v(202.56, 123.2) * mm});
            skLineSegment(sketch, "E196.MirrorCS", {"start": v(202.56, 135.9) * mm, "end": v(139.06, 135.9) * mm});
            skLineSegment(sketch, "E197.MirrorCS", {"start": v(139.06, 135.9) * mm, "end": v(139.06, 127) * mm});
            skLineSegment(sketch, "E198.MirrorCS", {"start": v(207.06, 125.05) * mm, "end": v(180.97, 98.97) * mm});
            skPoint(sketch, "E199.orphan", {"position": v(-180.97, 127) * mm});
            skLineSegment(sketch, "E200.trimOffspring", {"start": v(-128.59, 44.45) * mm, "end": v(-180.97, 44.45) * mm});
            skLineSegment(sketch, "E201.trimOffspring", {"start": v(74.61, 44.45) * mm, "end": v(26.99, 44.45) * mm});
            skLineSegment(sketch, "E202.trimOffspring", {"start": v(-26.99, 44.45) * mm, "end": v(-74.61, 44.45) * mm});
            skLineSegment(sketch, "E203.trimOffspring", {"start": v(-63.18, 15.88) * mm, "end": v(-38.42, 15.88) * mm});
            skLineSegment(sketch, "E204.trimOffspring", {"start": v(38.42, 15.88) * mm, "end": v(63.18, 15.88) * mm});
            skLineSegment(sketch, "E205.trimOffspring", {"start": v(140.02, 15.88) * mm, "end": v(214, 15.88) * mm});
            skLineSegment(sketch, "E206.0", {"start": v(-140.02, 38.1) * mm, "end": v(-182.25, 38.1) * mm});
            skLineSegment(sketch, "E206.1", {"start": v(132.72, 139.7) * mm, "end": v(132.72, 135.9) * mm});
            skLineSegment(sketch, "E206.2", {"start": v(202.56, 142.24) * mm, "end": v(198.75, 142.24) * mm});
            skArc(sketch, "E206.3", {"start": v(202.56, 142.24) * mm, "mid": v(214.3, 134.4) * mm, "end": v(211.55, 120.56) * mm});
            skLineSegment(sketch, "E206.4", {"start": v(211.55, 120.56) * mm, "end": v(188.81, 97.83) * mm});
            skLineSegment(sketch, "E206.5", {"start": v(130.18, 133.35) * mm, "end": v(14.6, 133.35) * mm});
            skLineSegment(sketch, "E206.6", {"start": v(-132.72, 137.45) * mm, "end": v(-132.72, 135.9) * mm});
            skLineSegment(sketch, "E206.7", {"start": v(-202.56, 142.24) * mm, "end": v(-198.75, 142.24) * mm});
            skArc(sketch, "E206.8", {"start": v(-202.56, 142.24) * mm, "mid": v(-214.3, 134.4) * mm, "end": v(-211.55, 120.56) * mm});
            skLineSegment(sketch, "E206.9", {"start": v(-211.55, 120.56) * mm, "end": v(-188.81, 97.83) * mm});
            skLineSegment(sketch, "E206.10", {"start": v(-187.32, 43.18) * mm, "end": v(-187.32, 94.24) * mm});
            skLineSegment(sketch, "E207.0", {"start": v(187.33, 43.18) * mm, "end": v(187.33, 94.24) * mm});
            skLineSegment(sketch, "E208.0", {"start": v(-134.94, 25.4) * mm, "end": v(-134.94, 33.02) * mm});
            skLineSegment(sketch, "E208.1", {"start": v(-134.94, 25.4) * mm, "end": v(-134.94, 20.96) * mm});
            skLineSegment(sketch, "E209.0", {"start": v(-33.34, 25.4) * mm, "end": v(-33.34, 20.96) * mm});
            skLineSegment(sketch, "E209.1", {"start": v(-68.26, 25.4) * mm, "end": v(-68.26, 20.96) * mm});
            skLineSegment(sketch, "E209.2", {"start": v(-68.26, 25.4) * mm, "end": v(-68.26, 33.02) * mm});
            skLineSegment(sketch, "E209.3", {"start": v(-38.42, 38.1) * mm, "end": v(-63.18, 38.1) * mm});
            skLineSegment(sketch, "E209.4", {"start": v(-33.34, 25.4) * mm, "end": v(-33.34, 33.02) * mm});
            skLineSegment(sketch, "E210.0", {"start": v(68.26, 25.4) * mm, "end": v(68.26, 20.96) * mm});
            skLineSegment(sketch, "E210.1", {"start": v(33.34, 25.4) * mm, "end": v(33.34, 20.96) * mm});
            skLineSegment(sketch, "E210.2", {"start": v(33.34, 25.4) * mm, "end": v(33.34, 33.02) * mm});
            skLineSegment(sketch, "E210.3", {"start": v(63.18, 38.1) * mm, "end": v(38.42, 38.1) * mm});
            skLineSegment(sketch, "E210.4", {"start": v(68.26, 25.4) * mm, "end": v(68.26, 33.02) * mm});
            skLineSegment(sketch, "E211.0", {"start": v(134.94, 25.4) * mm, "end": v(134.94, 20.96) * mm});
            skLineSegment(sketch, "E211.1", {"start": v(134.94, 25.4) * mm, "end": v(134.94, 33.02) * mm});
            skLineSegment(sketch, "E211.2", {"start": v(180.98, 38.1) * mm, "end": v(140.02, 38.1) * mm});
            skLineSegment(sketch, "E212", {"start": v(180.98, 38.1) * mm, "end": v(182.25, 38.1) * mm});
            skLineSegment(sketch, "E213", {"start": v(-193.67, 149.89) * mm, "end": v(-193.67, 147.32) * mm});
            skLineSegment(sketch, "E214", {"start": v(-161.93, 149.89) * mm, "end": v(-161.93, 147.03) * mm});
            skLineSegment(sketch, "E215.trimOffspring", {"start": v(-157.14, 142.24) * mm, "end": v(-137.5, 142.24) * mm});
            skLineSegment(sketch, "E216", {"start": v(161.93, 149.89) * mm, "end": v(161.93, 147.32) * mm});
            skLineSegment(sketch, "E217", {"start": v(193.67, 149.89) * mm, "end": v(193.67, 147.32) * mm});
            skLineSegment(sketch, "E218.trimOffspring", {"start": v(156.85, 142.24) * mm, "end": v(135.26, 142.24) * mm});
            skLineSegment(sketch, "E219", {"start": v(-9.53, 147.35) * mm, "end": v(-9.53, 138.43) * mm});
            skLineSegment(sketch, "E220", {"start": v(9.53, 147.35) * mm, "end": v(9.53, 138.43) * mm});
            skLineSegment(sketch, "E221.trimOffspring", {"start": v(-12.07, 149.89) * mm, "end": v(-13.34, 149.89) * mm});
            skLineSegment(sketch, "E222.trimOffspring", {"start": v(-14.6, 133.35) * mm, "end": v(-130.17, 133.35) * mm});
            skLineSegment(sketch, "E223.bottom", {"start": v(-166.37, 53.98) * mm, "end": v(166.37, 53.98) * mm});
            skLineSegment(sketch, "E223.top", {"start": v(-166.37, 117.48) * mm, "end": v(166.37, 117.48) * mm});
            skLineSegment(sketch, "E223.left", {"start": v(-171.45, 59.06) * mm, "end": v(-171.45, 112.4) * mm});
            skLineSegment(sketch, "E223.right", {"start": v(171.45, 59.06) * mm, "end": v(171.45, 112.4) * mm});
            skArc(sketch, "E224.filletArc", {"start": v(-156.85, 293.69) * mm, "mid": v(-160.44, 292.2) * mm, "end": v(-161.93, 288.6) * mm});
            skArc(sketch, "E225.filletArc", {"start": v(-15.88, 288.6) * mm, "mid": v(-17.36, 292.2) * mm, "end": v(-20.96, 293.69) * mm});
            skPoint(sketch, "E226.visualSharp", {"position": v(-161.93, 142.24) * mm});
            skArc(sketch, "E226.filletArc", {"start": v(-161.93, 147.03) * mm, "mid": v(-160.52, 143.64) * mm, "end": v(-157.14, 142.24) * mm});
            skPoint(sketch, "E227.visualSharp", {"position": v(-15.88, 149.89) * mm});
            skArc(sketch, "E227.filletArc", {"start": v(-15.88, 152.43) * mm, "mid": v(-15.13, 150.63) * mm, "end": v(-13.34, 149.89) * mm});
            skPoint(sketch, "E228.visualSharp", {"position": v(-132.72, 142.24) * mm});
            skArc(sketch, "E228.filletArc", {"start": v(-132.72, 137.45) * mm, "mid": v(-134.12, 140.84) * mm, "end": v(-137.5, 142.24) * mm});
            skPoint(sketch, "E229.visualSharp", {"position": v(-9.53, 149.89) * mm});
            skArc(sketch, "E229.filletArc", {"start": v(-9.53, 147.35) * mm, "mid": v(-10.27, 149.14) * mm, "end": v(-12.07, 149.89) * mm});
            skPoint(sketch, "E230.visualSharp", {"position": v(-9.53, 133.35) * mm});
            skArc(sketch, "E230.filletArc", {"start": v(-14.6, 133.35) * mm, "mid": v(-11.01, 134.84) * mm, "end": v(-9.53, 138.43) * mm});
            skPoint(sketch, "E231.visualSharp", {"position": v(-132.72, 133.35) * mm});
            skArc(sketch, "E231.filletArc", {"start": v(-132.71, 135.9) * mm, "mid": v(-131.97, 134.1) * mm, "end": v(-130.17, 133.35) * mm});
            skLineSegment(sketch, "E232", {"start": v(-214, 295.28) * mm, "end": v(-198.75, 295.28) * mm});
            skArc(sketch, "E233.filletArc", {"start": v(-193.67, 290.2) * mm, "mid": v(-195.16, 293.79) * mm, "end": v(-198.75, 295.28) * mm});
            skPoint(sketch, "E234.newPointB", {"position": v(-219.07, 307.98) * mm});
            skArc(sketch, "E234.filletArc", {"start": v(-214, 295.28) * mm, "mid": v(-217.59, 293.79) * mm, "end": v(-219.07, 290.2) * mm});
            skPoint(sketch, "E235.visualSharp", {"position": v(-193.67, 142.24) * mm});
            skArc(sketch, "E235.filletArc", {"start": v(-198.75, 142.24) * mm, "mid": v(-195.16, 143.73) * mm, "end": v(-193.67, 147.32) * mm});
            skPoint(sketch, "E236.visualSharp", {"position": v(-219.08, 15.88) * mm});
            skArc(sketch, "E236.filletArc", {"start": v(-219.07, 20.96) * mm, "mid": v(-217.59, 17.36) * mm, "end": v(-214, 15.88) * mm});
            skArc(sketch, "E237.filletArc", {"start": v(-140.02, 15.88) * mm, "mid": v(-136.43, 17.36) * mm, "end": v(-134.94, 20.96) * mm});
            skPoint(sketch, "E238.visualSharp", {"position": v(-134.94, 38.1) * mm});
            skArc(sketch, "E238.filletArc", {"start": v(-134.94, 33.02) * mm, "mid": v(-136.43, 36.61) * mm, "end": v(-140.02, 38.1) * mm});
            skPoint(sketch, "E239.visualSharp", {"position": v(-187.32, 38.1) * mm});
            skArc(sketch, "E239.filletArc", {"start": v(-187.32, 43.18) * mm, "mid": v(-185.84, 39.59) * mm, "end": v(-182.25, 38.1) * mm});
            skPoint(sketch, "E240.visualSharp", {"position": v(-187.32, 96.34) * mm});
            skArc(sketch, "E240.filletArc", {"start": v(-187.32, 94.24) * mm, "mid": v(-187.71, 96.18) * mm, "end": v(-188.81, 97.83) * mm});
            skPoint(sketch, "E241.visualSharp", {"position": v(-171.45, 117.48) * mm});
            skArc(sketch, "E241.filletArc", {"start": v(-166.37, 117.48) * mm, "mid": v(-169.96, 115.99) * mm, "end": v(-171.45, 112.4) * mm});
            skPoint(sketch, "E242.visualSharp", {"position": v(171.45, 117.48) * mm});
            skArc(sketch, "E242.filletArc", {"start": v(171.45, 112.4) * mm, "mid": v(169.96, 115.99) * mm, "end": v(166.37, 117.48) * mm});
            skPoint(sketch, "E243.visualSharp", {"position": v(171.45, 53.98) * mm});
            skArc(sketch, "E243.filletArc", {"start": v(166.37, 53.98) * mm, "mid": v(169.96, 55.46) * mm, "end": v(171.45, 59.06) * mm});
            skPoint(sketch, "E244.visualSharp", {"position": v(-171.45, 53.98) * mm});
            skArc(sketch, "E244.filletArc", {"start": v(-171.45, 59.06) * mm, "mid": v(-169.96, 55.46) * mm, "end": v(-166.37, 53.98) * mm});
            skArc(sketch, "E245.filletArc", {"start": v(-68.26, 20.96) * mm, "mid": v(-66.77, 17.36) * mm, "end": v(-63.18, 15.88) * mm});
            skArc(sketch, "E246.filletArc", {"start": v(-38.42, 15.88) * mm, "mid": v(-34.83, 17.36) * mm, "end": v(-33.34, 20.96) * mm});
            skPoint(sketch, "E247.visualSharp", {"position": v(-33.34, 38.1) * mm});
            skArc(sketch, "E247.filletArc", {"start": v(-33.34, 33.02) * mm, "mid": v(-34.83, 36.61) * mm, "end": v(-38.42, 38.1) * mm});
            skPoint(sketch, "E248.visualSharp", {"position": v(-68.26, 38.1) * mm});
            skArc(sketch, "E248.filletArc", {"start": v(-63.18, 38.1) * mm, "mid": v(-66.77, 36.61) * mm, "end": v(-68.26, 33.02) * mm});
            skArc(sketch, "E249.filletArc", {"start": v(33.34, 20.96) * mm, "mid": v(34.83, 17.36) * mm, "end": v(38.42, 15.88) * mm});
            skArc(sketch, "E250.filletArc", {"start": v(63.18, 15.88) * mm, "mid": v(66.77, 17.36) * mm, "end": v(68.26, 20.96) * mm});
            skPoint(sketch, "E251.visualSharp", {"position": v(68.26, 38.1) * mm});
            skArc(sketch, "E251.filletArc", {"start": v(68.26, 33.02) * mm, "mid": v(66.77, 36.61) * mm, "end": v(63.18, 38.1) * mm});
            skPoint(sketch, "E252.visualSharp", {"position": v(33.34, 38.1) * mm});
            skArc(sketch, "E252.filletArc", {"start": v(38.42, 38.1) * mm, "mid": v(34.83, 36.61) * mm, "end": v(33.34, 33.02) * mm});
            skArc(sketch, "E253.filletArc", {"start": v(134.94, 20.96) * mm, "mid": v(136.43, 17.36) * mm, "end": v(140.02, 15.88) * mm});
            skPoint(sketch, "E254.visualSharp", {"position": v(134.94, 38.1) * mm});
            skArc(sketch, "E254.filletArc", {"start": v(140.02, 38.1) * mm, "mid": v(136.43, 36.61) * mm, "end": v(134.94, 33.02) * mm});
            skPoint(sketch, "E255.visualSharp", {"position": v(187.33, 38.1) * mm});
            skArc(sketch, "E255.filletArc", {"start": v(182.25, 38.1) * mm, "mid": v(185.84, 39.59) * mm, "end": v(187.33, 43.18) * mm});
            skPoint(sketch, "E256.visualSharp", {"position": v(219.08, 15.88) * mm});
            skArc(sketch, "E256.filletArc", {"start": v(214, 15.88) * mm, "mid": v(217.59, 17.36) * mm, "end": v(219.08, 20.96) * mm});
            skArc(sketch, "E257.filletArc", {"start": v(188.81, 97.83) * mm, "mid": v(187.71, 96.18) * mm, "end": v(187.33, 94.24) * mm});
            skPoint(sketch, "E258.visualSharp", {"position": v(193.67, 142.24) * mm});
            skArc(sketch, "E258.filletArc", {"start": v(193.67, 147.32) * mm, "mid": v(195.16, 143.73) * mm, "end": v(198.75, 142.24) * mm});
            skLineSegment(sketch, "E259", {"start": v(219.08, 307.98) * mm, "end": v(219.08, 295.28) * mm});
            skLineSegment(sketch, "E260", {"start": v(214, 295.28) * mm, "end": v(198.75, 295.28) * mm});
            skArc(sketch, "E261.filletArc", {"start": v(198.75, 295.28) * mm, "mid": v(195.16, 293.79) * mm, "end": v(193.67, 290.2) * mm});
            skPoint(sketch, "E262.newPointB", {"position": v(219.07, 307.98) * mm});
            skArc(sketch, "E262.filletArc", {"start": v(219.07, 290.2) * mm, "mid": v(217.59, 293.79) * mm, "end": v(214, 295.28) * mm});
            skLineSegment(sketch, "E263", {"start": v(168.27, 307.98) * mm, "end": v(168.27, 295.28) * mm});
            skLineSegment(sketch, "E264", {"start": v(156.85, 295.28) * mm, "end": v(20.96, 295.28) * mm});
            skArc(sketch, "E265.filletArc", {"start": v(161.93, 290.2) * mm, "mid": v(160.44, 293.79) * mm, "end": v(156.85, 295.28) * mm});
            skArc(sketch, "E266.filletArc", {"start": v(20.96, 295.28) * mm, "mid": v(17.36, 293.79) * mm, "end": v(15.88, 290.2) * mm});
            skPoint(sketch, "E267.visualSharp", {"position": v(161.93, 142.24) * mm});
            skArc(sketch, "E267.filletArc", {"start": v(156.85, 142.24) * mm, "mid": v(160.44, 143.73) * mm, "end": v(161.93, 147.32) * mm});
            skPoint(sketch, "E268.visualSharp", {"position": v(132.71, 142.24) * mm});
            skArc(sketch, "E268.filletArc", {"start": v(135.26, 142.24) * mm, "mid": v(133.46, 141.5) * mm, "end": v(132.72, 139.7) * mm});
            skPoint(sketch, "E269.visualSharp", {"position": v(15.88, 149.89) * mm});
            skArc(sketch, "E269.filletArc", {"start": v(13.34, 149.89) * mm, "mid": v(15.13, 150.63) * mm, "end": v(15.88, 152.43) * mm});
            skPoint(sketch, "E270.visualSharp", {"position": v(132.72, 133.35) * mm});
            skArc(sketch, "E270.filletArc", {"start": v(130.18, 133.35) * mm, "mid": v(131.97, 134.1) * mm, "end": v(132.72, 135.9) * mm});
            skPoint(sketch, "E271.visualSharp", {"position": v(9.53, 149.89) * mm});
            skArc(sketch, "E271.filletArc", {"start": v(12.07, 149.89) * mm, "mid": v(10.27, 149.14) * mm, "end": v(9.53, 147.35) * mm});
            skPoint(sketch, "E272.visualSharp", {"position": v(9.53, 133.35) * mm});
            skArc(sketch, "E272.filletArc", {"start": v(9.53, 138.43) * mm, "mid": v(11.01, 134.84) * mm, "end": v(14.6, 133.35) * mm});
            skSolve(sketch);
        }
        {
            var Q0;
            Q0=makeQuery(id+"F10.imprint","IMPRINT",FACE,{"disambiguationData":[TD([[makeQuery(id+"F10.imprint","IMPRINT",EDGE,{"derivedFrom":sQuery(id+"F10.wireOp",EDGE,"E181")}),1.0]])]});
            var Q1;
            Q1=makeQuery(id+"F10.imprint","IMPRINT",FACE,{"disambiguationData":[TD([[makeQuery(id+"F10.imprint","IMPRINT",EDGE,{"derivedFrom":sQuery(id+"F10.wireOp",EDGE,"E182.MirrorCS")}),-1.0]])]});
            var Q2;
            Q2=makeQuery(id+"F10.imprint","IMPRINT",FACE,{"disambiguationData":[TD([[makeQuery(id+"F10.imprint","IMPRINT",EDGE,{"derivedFrom":sQuery(id+"F10.wireOp",EDGE,"E186")}),-1.0]])]});
            var Q3;
            Q3=makeQuery(id+"F10.imprint","IMPRINT",FACE,{"disambiguationData":[TD([[makeQuery(id+"F10.imprint","IMPRINT",EDGE,{"derivedFrom":sQuery(id+"F10.wireOp",EDGE,"E187.1")}),1.0]])]});
            var Q4;
            Q4=makeQuery(id+"F10.imprint","IMPRINT",FACE,{"disambiguationData":[TD([[makeQuery(id+"F10.imprint","IMPRINT",EDGE,{"derivedFrom":sQuery(id+"F10.wireOp",EDGE,"E204.trimOffspring")}),1.0]])]});
            var Q5;
            Q5=makeQuery(id+"F10.imprint","IMPRINT",FACE,{"disambiguationData":[TD([[makeQuery(id+"F10.imprint","IMPRINT",EDGE,{"derivedFrom":sQuery(id+"F10.wireOp",EDGE,"E223.top")}),-1.0]])]});
            var Q6;
            Q6=makeQuery(id+"F10.imprint","IMPRINT",FACE,{"disambiguationData":[TD([[makeQuery(id+"F10.imprint","IMPRINT",EDGE,{"derivedFrom":sQuery(id+"F10.wireOp",EDGE,"E203.trimOffspring")}),1.0]])]});
            extrude(context, id + "F11", {"entities" : qUnion([Q0, Q1, Q2, Q3, Q4, Q5, Q6]), "operationType" : NewBodyOperationType.REMOVE, "endBound" : BoundingType.SYMMETRIC, "oppositeDirection" : true, "depth" : 2540 * mm, "offsetDistance" : 25.4 * mm});
        }
        {
            var Q0;
            Q0=makeQuery(id+"F0.imprint","IMPRINT",FACE,{"disambiguationData":[TD([[makeQuery(id+"F0.imprint","IMPRINT",EDGE,{"derivedFrom":sQuery(id+"F0.wireOp",EDGE,"E0.bottom")}),-1.0]])]});
            var sketch = newSketch(context, id + "F12", { "sketchPlane" : qUnion([Q0])});
            skLineSegment(sketch, "E273.bottom", {"start": v(-231.78, 231.77) * mm, "end": v(231.77, 231.77) * mm});
            skLineSegment(sketch, "E273.top", {"start": v(-231.78, -231.78) * mm, "end": v(231.77, -231.78) * mm});
            skLineSegment(sketch, "E273.left", {"start": v(-231.78, 231.77) * mm, "end": v(-231.77, -231.78) * mm});
            skLineSegment(sketch, "E273.right", {"start": v(231.77, 231.78) * mm, "end": v(231.77, -231.78) * mm});
            skPoint(sketch, "E274.orphan", {"position": v(-103.19, -206.37) * mm});
            skLineSegment(sketch, "E275.0", {"start": v(-187.33, 193.67) * mm, "end": v(-122.24, 193.67) * mm});
            skLineSegment(sketch, "E275.1", {"start": v(-193.68, 187.32) * mm, "end": v(-193.68, 19.05) * mm});
            skLineSegment(sketch, "E275.2", {"start": v(-122.24, 12.7) * mm, "end": v(-187.33, 12.7) * mm});
            skLineSegment(sketch, "E275.3", {"start": v(-115.89, 187.32) * mm, "end": v(-115.89, 19.05) * mm});
            skPoint(sketch, "E276.visualSharp", {"position": v(-115.89, 12.7) * mm});
            skArc(sketch, "E276.filletArc", {"start": v(-122.24, 12.7) * mm, "mid": v(-117.75, 14.56) * mm, "end": v(-115.89, 19.05) * mm});
            skPoint(sketch, "E277.visualSharp", {"position": v(-115.89, 193.67) * mm});
            skArc(sketch, "E277.filletArc", {"start": v(-115.89, 187.32) * mm, "mid": v(-117.75, 191.82) * mm, "end": v(-122.24, 193.67) * mm});
            skPoint(sketch, "E278.visualSharp", {"position": v(-193.68, 193.67) * mm});
            skArc(sketch, "E278.filletArc", {"start": v(-187.33, 193.67) * mm, "mid": v(-191.82, 191.82) * mm, "end": v(-193.68, 187.32) * mm});
            skPoint(sketch, "E279.visualSharp", {"position": v(-193.68, 12.7) * mm});
            skArc(sketch, "E279.filletArc", {"start": v(-193.68, 19.05) * mm, "mid": v(-191.82, 14.56) * mm, "end": v(-187.33, 12.7) * mm});
            skArc(sketch, "E280.MirrorCS", {"start": v(-90.49, 187.32) * mm, "mid": v(-88.63, 191.82) * mm, "end": v(-84.14, 193.67) * mm});
            skArc(sketch, "E281.MirrorCS", {"start": v(-19.05, 193.67) * mm, "mid": v(-14.56, 191.82) * mm, "end": v(-12.7, 187.32) * mm});
            skLineSegment(sketch, "E282.MirrorCS", {"start": v(-12.7, 187.32) * mm, "end": v(-12.7, 19.05) * mm});
            skPoint(sketch, "E283.MirrorP", {"position": v(-90.49, 12.7) * mm});
            skArc(sketch, "E284.MirrorCS", {"start": v(-12.7, 19.05) * mm, "mid": v(-14.56, 14.56) * mm, "end": v(-19.05, 12.7) * mm});
            skPoint(sketch, "E285.MirrorP", {"position": v(-90.49, 193.67) * mm});
            skPoint(sketch, "E286.MirrorP", {"position": v(-12.7, 193.67) * mm});
            skLineSegment(sketch, "E287.MirrorCS", {"start": v(-19.05, 193.68) * mm, "end": v(-84.14, 193.68) * mm});
            skLineSegment(sketch, "E288.MirrorCS", {"start": v(-84.14, 12.7) * mm, "end": v(-19.05, 12.7) * mm});
            skLineSegment(sketch, "E289.MirrorCS", {"start": v(-90.49, 187.32) * mm, "end": v(-90.49, 19.05) * mm});
            skPoint(sketch, "E290.MirrorP", {"position": v(-12.7, 12.7) * mm});
            skArc(sketch, "E291.MirrorCS", {"start": v(-84.14, 12.7) * mm, "mid": v(-88.63, 14.56) * mm, "end": v(-90.49, 19.05) * mm});
            skLineSegment(sketch, "E292.MirrorCS", {"start": v(193.67, 187.33) * mm, "end": v(193.68, 19.05) * mm});
            skPoint(sketch, "E293.MirrorP", {"position": v(193.68, 12.7) * mm});
            skPoint(sketch, "E294.MirrorP", {"position": v(193.67, 193.68) * mm});
            skArc(sketch, "E295.MirrorCS", {"start": v(19.05, 193.68) * mm, "mid": v(14.56, 191.82) * mm, "end": v(12.7, 187.33) * mm});
            skArc(sketch, "E296.MirrorCS", {"start": v(193.68, 19.05) * mm, "mid": v(191.82, 14.56) * mm, "end": v(187.33, 12.7) * mm});
            skArc(sketch, "E297.MirrorCS", {"start": v(115.89, 187.33) * mm, "mid": v(117.75, 191.82) * mm, "end": v(122.24, 193.68) * mm});
            skLineSegment(sketch, "E298.MirrorCS", {"start": v(115.89, 187.33) * mm, "end": v(115.89, 19.05) * mm});
            skLineSegment(sketch, "E299.MirrorCS", {"start": v(122.24, 12.7) * mm, "end": v(187.33, 12.7) * mm});
            skPoint(sketch, "E300.MirrorP", {"position": v(12.7, 12.7) * mm});
            skPoint(sketch, "E301.MirrorP", {"position": v(90.49, 193.68) * mm});
            skPoint(sketch, "E302.MirrorP", {"position": v(90.49, 12.7) * mm});
            skArc(sketch, "E303.MirrorCS", {"start": v(84.14, 12.7) * mm, "mid": v(88.63, 14.56) * mm, "end": v(90.49, 19.05) * mm});
            skLineSegment(sketch, "E304.MirrorCS", {"start": v(90.49, 187.33) * mm, "end": v(90.49, 19.05) * mm});
            skArc(sketch, "E305.MirrorCS", {"start": v(12.7, 19.05) * mm, "mid": v(14.56, 14.56) * mm, "end": v(19.05, 12.7) * mm});
            skLineSegment(sketch, "E306.MirrorCS", {"start": v(19.05, 193.68) * mm, "end": v(84.14, 193.68) * mm});
            skPoint(sketch, "E307.MirrorP", {"position": v(115.89, 12.7) * mm});
            skPoint(sketch, "E308.MirrorP", {"position": v(115.89, 193.68) * mm});
            skArc(sketch, "E309.MirrorCS", {"start": v(90.49, 187.33) * mm, "mid": v(88.63, 191.82) * mm, "end": v(84.14, 193.68) * mm});
            skArc(sketch, "E310.MirrorCS", {"start": v(187.32, 193.68) * mm, "mid": v(191.82, 191.82) * mm, "end": v(193.67, 187.33) * mm});
            skArc(sketch, "E311.MirrorCS", {"start": v(122.24, 12.7) * mm, "mid": v(117.75, 14.56) * mm, "end": v(115.89, 19.05) * mm});
            skPoint(sketch, "E312.MirrorP", {"position": v(12.7, 193.67) * mm});
            skLineSegment(sketch, "E313.MirrorCS", {"start": v(187.32, 193.68) * mm, "end": v(122.24, 193.68) * mm});
            skLineSegment(sketch, "E314.MirrorCS", {"start": v(84.14, 12.7) * mm, "end": v(19.05, 12.7) * mm});
            skLineSegment(sketch, "E315.MirrorCS", {"start": v(12.7, 187.32) * mm, "end": v(12.7, 19.05) * mm});
            skPoint(sketch, "E316.MirrorP", {"position": v(90.49, -12.7) * mm});
            skPoint(sketch, "E317.MirrorP", {"position": v(-115.89, -12.7) * mm});
            skArc(sketch, "E318.MirrorCS", {"start": v(-19.05, -193.67) * mm, "mid": v(-14.56, -191.82) * mm, "end": v(-12.7, -187.32) * mm});
            skLineSegment(sketch, "E319.MirrorCS", {"start": v(84.14, -12.7) * mm, "end": v(19.05, -12.7) * mm});
            skArc(sketch, "E320.MirrorCS", {"start": v(122.24, -12.7) * mm, "mid": v(117.75, -14.56) * mm, "end": v(115.89, -19.05) * mm});
            skPoint(sketch, "E321.MirrorP", {"position": v(193.68, -12.7) * mm});
            skLineSegment(sketch, "E322.MirrorCS", {"start": v(-12.7, -187.32) * mm, "end": v(-12.7, -19.05) * mm});
            skPoint(sketch, "E323.MirrorP", {"position": v(12.7, -193.67) * mm});
            skPoint(sketch, "E324.MirrorP", {"position": v(-90.49, -193.67) * mm});
            skLineSegment(sketch, "E325.MirrorCS", {"start": v(90.49, -187.33) * mm, "end": v(90.49, -19.05) * mm});
            skArc(sketch, "E326.MirrorCS", {"start": v(-187.33, -193.67) * mm, "mid": v(-191.82, -191.82) * mm, "end": v(-193.68, -187.32) * mm});
            skPoint(sketch, "E327.MirrorP", {"position": v(12.7, -12.7) * mm});
            skLineSegment(sketch, "E328.MirrorCS", {"start": v(-90.49, -187.32) * mm, "end": v(-90.49, -19.05) * mm});
            skLineSegment(sketch, "E329.MirrorCS", {"start": v(115.89, -187.33) * mm, "end": v(115.89, -19.05) * mm});
            skLineSegment(sketch, "E330.MirrorCS", {"start": v(-115.89, -187.32) * mm, "end": v(-115.89, -19.05) * mm});
            skPoint(sketch, "E331.MirrorP", {"position": v(-115.89, -193.67) * mm});
            skArc(sketch, "E332.MirrorCS", {"start": v(90.49, -187.33) * mm, "mid": v(88.63, -191.82) * mm, "end": v(84.14, -193.67) * mm});
            skPoint(sketch, "E333.MirrorP", {"position": v(-193.68, -12.7) * mm});
            skArc(sketch, "E334.MirrorCS", {"start": v(19.05, -193.67) * mm, "mid": v(14.56, -191.82) * mm, "end": v(12.7, -187.32) * mm});
            skPoint(sketch, "E335.MirrorP", {"position": v(90.49, -193.68) * mm});
            skArc(sketch, "E336.MirrorCS", {"start": v(-84.14, -12.7) * mm, "mid": v(-88.63, -14.56) * mm, "end": v(-90.49, -19.05) * mm});
            skPoint(sketch, "E337.MirrorP", {"position": v(-12.7, -12.7) * mm});
            skArc(sketch, "E338.MirrorCS", {"start": v(-90.49, -187.32) * mm, "mid": v(-88.63, -191.82) * mm, "end": v(-84.14, -193.67) * mm});
            skLineSegment(sketch, "E339.MirrorCS", {"start": v(19.05, -193.67) * mm, "end": v(84.14, -193.68) * mm});
            skLineSegment(sketch, "E340.MirrorCS", {"start": v(187.32, -193.68) * mm, "end": v(122.24, -193.68) * mm});
            skArc(sketch, "E341.MirrorCS", {"start": v(187.32, -193.68) * mm, "mid": v(191.82, -191.82) * mm, "end": v(193.67, -187.33) * mm});
            skArc(sketch, "E342.MirrorCS", {"start": v(84.14, -12.7) * mm, "mid": v(88.63, -14.56) * mm, "end": v(90.49, -19.05) * mm});
            skArc(sketch, "E343.MirrorCS", {"start": v(-115.89, -187.32) * mm, "mid": v(-117.75, -191.82) * mm, "end": v(-122.24, -193.67) * mm});
            skPoint(sketch, "E344.MirrorP", {"position": v(-193.68, -193.67) * mm});
            skArc(sketch, "E345.MirrorCS", {"start": v(115.89, -187.33) * mm, "mid": v(117.75, -191.82) * mm, "end": v(122.24, -193.68) * mm});
            skLineSegment(sketch, "E346.MirrorCS", {"start": v(-84.14, -12.7) * mm, "end": v(-19.05, -12.7) * mm});
            skPoint(sketch, "E347.MirrorP", {"position": v(115.89, -193.68) * mm});
            skLineSegment(sketch, "E348.MirrorCS", {"start": v(193.67, -187.33) * mm, "end": v(193.68, -19.05) * mm});
            skLineSegment(sketch, "E349.MirrorCS", {"start": v(-187.33, -193.67) * mm, "end": v(-122.24, -193.67) * mm});
            skLineSegment(sketch, "E350.MirrorCS", {"start": v(12.7, -187.32) * mm, "end": v(12.7, -19.05) * mm});
            skPoint(sketch, "E351.MirrorP", {"position": v(193.67, -193.68) * mm});
            skArc(sketch, "E352.MirrorCS", {"start": v(-12.7, -19.05) * mm, "mid": v(-14.56, -14.56) * mm, "end": v(-19.05, -12.7) * mm});
            skArc(sketch, "E353.MirrorCS", {"start": v(-193.68, -19.05) * mm, "mid": v(-191.82, -14.56) * mm, "end": v(-187.33, -12.7) * mm});
            skPoint(sketch, "E354.MirrorP", {"position": v(-12.7, -193.67) * mm});
            skArc(sketch, "E355.MirrorCS", {"start": v(12.7, -19.05) * mm, "mid": v(14.56, -14.56) * mm, "end": v(19.05, -12.7) * mm});
            skLineSegment(sketch, "E356.MirrorCS", {"start": v(-193.68, -187.32) * mm, "end": v(-193.68, -19.05) * mm});
            skLineSegment(sketch, "E357.MirrorCS", {"start": v(122.24, -12.7) * mm, "end": v(187.33, -12.7) * mm});
            skPoint(sketch, "E358.MirrorP", {"position": v(-90.49, -12.7) * mm});
            skArc(sketch, "E359.MirrorCS", {"start": v(-122.24, -12.7) * mm, "mid": v(-117.75, -14.56) * mm, "end": v(-115.89, -19.05) * mm});
            skLineSegment(sketch, "E360.MirrorCS", {"start": v(-122.24, -12.7) * mm, "end": v(-187.33, -12.7) * mm});
            skPoint(sketch, "E361.MirrorP", {"position": v(115.89, -12.7) * mm});
            skArc(sketch, "E362.MirrorCS", {"start": v(193.68, -19.05) * mm, "mid": v(191.82, -14.56) * mm, "end": v(187.33, -12.7) * mm});
            skLineSegment(sketch, "E363.MirrorCS", {"start": v(-19.05, -193.67) * mm, "end": v(-84.14, -193.67) * mm});
            skPoint(sketch, "E364.end.orphan", {"position": v(-103.19, 0) * mm});
            skPoint(sketch, "E365.0.end.orphan", {"position": v(-103.19, 206.37) * mm});
            skPoint(sketch, "E366.orphan", {"position": v(0, 206.37) * mm});
            skPoint(sketch, "E365.3.start.orphan", {"position": v(206.37, 206.37) * mm});
            skPoint(sketch, "E365.1.end.orphan", {"position": v(-206.38, 0) * mm});
            skPoint(sketch, "E365.1.start.orphan", {"position": v(-206.38, 206.37) * mm});
            skPoint(sketch, "E365.2.start.orphan", {"position": v(-206.38, -206.37) * mm});
            skSolve(sketch);
        }
        {
            var Q0;
            Q0 = qSketchRegion(id + "F12", true);
            extrude(context, id + "F13", {"entities" : qUnion([Q0]), "depth" : 3.17 * mm, "offsetDistance" : 25.4 * mm});
        }
        {
            var Q0;
            Q0=makeQuery(id+"F3.opExtrude","SWEPT_FACE",FACE,{"disambiguationData":[OSD([sQuery(id+"F0.wireOp",EDGE,"E21.MirrorCS")])]});
            var sketch = newSketch(context, id + "F14", { "sketchPlane" : qUnion([Q0])});
            skLineSegment(sketch, "E367", {"start": v(238.13, 307.98) * mm, "end": v(225.43, 307.98) * mm});
            skLineSegment(sketch, "E368", {"start": v(225.43, 307.98) * mm, "end": v(225.43, -3.18) * mm});
            skLineSegment(sketch, "E369", {"start": v(225.43, 152.4) * mm, "end": v(258.16, 152.4) * mm});
            skLineSegment(sketch, "E370", {"start": v(225.43, 152.4) * mm, "end": v(225.43, 177.8) * mm});
            skLineSegment(sketch, "E371", {"start": v(225.43, 177.8) * mm, "end": v(225.43, 228.6) * mm});
            skLineSegment(sketch, "E372", {"start": v(225.43, 228.6) * mm, "end": v(225.43, 279.4) * mm});
            skLineSegment(sketch, "E373.MirrorCS", {"start": v(225.43, 127) * mm, "end": v(225.43, 76.2) * mm});
            skLineSegment(sketch, "E374.MirrorCS", {"start": v(225.43, 76.2) * mm, "end": v(225.43, 25.4) * mm});
            skLineSegment(sketch, "E375", {"start": v(0, 0) * mm, "end": v(0, -196.26) * mm});
            skLineSegment(sketch, "E376.MirrorCS", {"start": v(-238.13, 307.98) * mm, "end": v(-225.43, 307.98) * mm});
            skLineSegment(sketch, "E377.MirrorCS", {"start": v(-225.43, 307.98) * mm, "end": v(-225.43, -3.18) * mm});
            skLineSegment(sketch, "E378.MirrorCS", {"start": v(-225.43, 152.4) * mm, "end": v(-258.16, 152.4) * mm});
            skLineSegment(sketch, "E379.MirrorCS", {"start": v(-225.43, 152.4) * mm, "end": v(-225.43, 177.8) * mm});
            skLineSegment(sketch, "E380.MirrorCS", {"start": v(-225.43, 177.8) * mm, "end": v(-225.43, 228.6) * mm});
            skLineSegment(sketch, "E381.MirrorCS", {"start": v(-225.43, 228.6) * mm, "end": v(-225.43, 279.4) * mm});
            skLineSegment(sketch, "E382.MirrorCS", {"start": v(-225.43, 127) * mm, "end": v(-225.43, 76.2) * mm});
            skLineSegment(sketch, "E383.MirrorCS", {"start": v(-225.43, 76.2) * mm, "end": v(-225.43, 25.4) * mm});
            skSolve(sketch);
        }
        {
            var Q0;
            Q0=sQuery(id+"F14.wireOp",VERTEX,"E372.end");
            var Q1;
            Q1=sQuery(id+"F14.wireOp",VERTEX,"E372.start");
            var Q2;
            Q2=sQuery(id+"F14.wireOp",VERTEX,"E371.start");
            var Q3;
            Q3=sQuery(id+"F14.wireOp",VERTEX,"E373.MirrorCS.start");
            var Q4;
            Q4=sQuery(id+"F14.wireOp",VERTEX,"E374.MirrorCS.start");
            var Q5;
            Q5=sQuery(id+"F14.wireOp",VERTEX,"E374.MirrorCS.end");
            var Q6;
            Q6=sQuery(id+"F14.wireOp",VERTEX,"E379.MirrorCS.end");
            var Q7;
            Q7=sQuery(id+"F14.wireOp",VERTEX,"E381.MirrorCS.end");
            var Q8;
            Q8=sQuery(id+"F14.wireOp",VERTEX,"E380.MirrorCS.end");
            var Q9;
            Q9=sQuery(id+"F14.wireOp",VERTEX,"E383.MirrorCS.end");
            var Q10;
            Q10=sQuery(id+"F14.wireOp",VERTEX,"E382.MirrorCS.start");
            var Q11;
            Q11=sQuery(id+"F14.wireOp",VERTEX,"E382.MirrorCS.end");
            var Q12;
            Q12=makeQuery(id+"F2.opExtrude","SWEPT_BODY",BODY,{"disambiguationData":[OSD([sQuery(id+"F0.wireOp",EDGE,"E0.bottom"),sQuery(id+"F0.wireOp",EDGE,"E1.0"),sQuery(id+"F0.wireOp",EDGE,"E1.1"),sQuery(id+"F0.wireOp",EDGE,"E1.2"),sQuery(id+"F0.wireOp",EDGE,"E4.MirrorCS"),sQuery(id+"F0.wireOp",EDGE,"E5.MirrorCS")])]});
            var Q13;
            Q13=makeQuery(id+"F2.opExtrude","SWEPT_BODY",BODY,{"disambiguationData":[OSD([sQuery(id+"F0.wireOp",EDGE,"E0.top"),sQuery(id+"F0.wireOp",EDGE,"E1.0"),sQuery(id+"F0.wireOp",EDGE,"E1.2"),sQuery(id+"F0.wireOp",EDGE,"E1.3"),sQuery(id+"F0.wireOp",EDGE,"E2"),sQuery(id+"F0.wireOp",EDGE,"E3.MirrorCS")])]});
            var Q14;
            Q14=makeQuery(id+"F3.opExtrude","SWEPT_BODY",BODY,{"disambiguationData":[OSD([sQuery(id+"F0.wireOp",EDGE,"E1.0"),sQuery(id+"F0.wireOp",EDGE,"E1.1"),sQuery(id+"F0.wireOp",EDGE,"E19.MirrorCS"),sQuery(id+"F0.wireOp",EDGE,"E20.MirrorCS"),sQuery(id+"F0.wireOp",EDGE,"E21.MirrorCS"),sQuery(id+"F0.wireOp",EDGE,"E22.MirrorCS")])]});
            var Q15;
            Q15=makeQuery(id+"F3.opExtrude","SWEPT_BODY",BODY,{"disambiguationData":[OSD([sQuery(id+"F0.wireOp",EDGE,"E1.0"),sQuery(id+"F0.wireOp",EDGE,"E1.3"),sQuery(id+"F0.wireOp",EDGE,"E11.MirrorCS"),sQuery(id+"F0.wireOp",EDGE,"E12.MirrorCS"),sQuery(id+"F0.wireOp",EDGE,"E13.MirrorCS"),sQuery(id+"F0.wireOp",EDGE,"E14.MirrorCS")])]});
            var Q16;
            Q16=makeQuery(id+"F3.opExtrude","SWEPT_BODY",BODY,{"disambiguationData":[OSD([sQuery(id+"F0.wireOp",EDGE,"E1.1"),sQuery(id+"F0.wireOp",EDGE,"E1.2"),sQuery(id+"F0.wireOp",EDGE,"E15.MirrorCS"),sQuery(id+"F0.wireOp",EDGE,"E16.MirrorCS"),sQuery(id+"F0.wireOp",EDGE,"E17.MirrorCS"),sQuery(id+"F0.wireOp",EDGE,"E18.MirrorCS")])]});
            var Q17;
            Q17=makeQuery(id+"F3.opExtrude","SWEPT_BODY",BODY,{"disambiguationData":[OSD([sQuery(id+"F0.wireOp",EDGE,"E1.2"),sQuery(id+"F0.wireOp",EDGE,"E1.3"),sQuery(id+"F0.wireOp",EDGE,"E7"),sQuery(id+"F0.wireOp",EDGE,"E8"),sQuery(id+"F0.wireOp",EDGE,"E9"),sQuery(id+"F0.wireOp",EDGE,"E10")])]});
            hole(context, id + "F15", {"style" : HoleStyle.SIMPLE, "endStyle" : HoleEndStyle.THROUGH, "standardTappedOrClearance" : lookupTablePath({ "standard" : "ANSI", "fit" : "Close", "size" : "#4", "type" : "Clearance" }), "standardBlindInLast" : lookupTablePath({ "fit" : "Close", "standard" : "ANSI", "size" : "#4", "type" : "Clearance" }), "holeDiameter" : 2.95 * mm, "majorDiameter" : 6.35 * mm, "isTappedThrough" : true, "tappedDepth" : 12.7 * mm, "tapClearance" : 3, "locations" : qUnion([Q0, Q1, Q2, Q3, Q4, Q5, Q6, Q7, Q8, Q9, Q10, Q11]), "scope" : qUnion([Q12, Q13, Q14, Q15, Q16, Q17])});
        }
        {
            var Q0;
            Q0=makeQuery(id+"F3.opExtrude","SWEPT_FACE",FACE,{"disambiguationData":[OSD([sQuery(id+"F0.wireOp",EDGE,"E22.MirrorCS")])]});
            var sketch = newSketch(context, id + "F16", { "sketchPlane" : qUnion([Q0])});
            skLineSegment(sketch, "E384", {"start": v(-238.12, 307.98) * mm, "end": v(-225.42, 307.98) * mm});
            skLineSegment(sketch, "E385", {"start": v(-225.42, 307.98) * mm, "end": v(-225.42, 0) * mm});
            skLineSegment(sketch, "E386", {"start": v(-225.42, 153.99) * mm, "end": v(-271.28, 153.99) * mm});
            skLineSegment(sketch, "E387", {"start": v(-225.42, 153.99) * mm, "end": v(-225.42, 204.79) * mm});
            skLineSegment(sketch, "E388", {"start": v(-225.42, 204.79) * mm, "end": v(-225.42, 255.59) * mm});
            skLineSegment(sketch, "E389", {"start": v(-225.42, 153.99) * mm, "end": v(-225.42, 103.19) * mm});
            skLineSegment(sketch, "E390", {"start": v(-225.42, 103.19) * mm, "end": v(-225.42, 52.39) * mm});
            skLineSegment(sketch, "E391", {"start": v(0, 0) * mm, "end": v(0, -160.54) * mm});
            skLineSegment(sketch, "E392.MirrorCS", {"start": v(225.42, 204.79) * mm, "end": v(225.42, 255.59) * mm});
            skLineSegment(sketch, "E393.MirrorCS", {"start": v(225.42, 153.99) * mm, "end": v(225.42, 103.19) * mm});
            skLineSegment(sketch, "E394.MirrorCS", {"start": v(225.42, 103.19) * mm, "end": v(225.42, 52.39) * mm});
            skLineSegment(sketch, "E395.MirrorCS", {"start": v(238.12, 307.98) * mm, "end": v(225.42, 307.98) * mm});
            skLineSegment(sketch, "E396.MirrorCS", {"start": v(225.42, 307.98) * mm, "end": v(225.42, 0) * mm});
            skLineSegment(sketch, "E397.MirrorCS", {"start": v(225.42, 153.99) * mm, "end": v(271.28, 153.99) * mm});
            skLineSegment(sketch, "E398.MirrorCS", {"start": v(225.42, 153.99) * mm, "end": v(225.42, 204.79) * mm});
            skSolve(sketch);
        }
        {
            var Q0;
            Q0=sQuery(id+"F16.wireOp",VERTEX,"E388.end");
            var Q1;
            Q1=sQuery(id+"F16.wireOp",VERTEX,"E387.end");
            var Q2;
            Q2=sQuery(id+"F16.wireOp",VERTEX,"E387.start");
            var Q3;
            Q3=sQuery(id+"F16.wireOp",VERTEX,"E390.end");
            var Q4;
            Q4=sQuery(id+"F16.wireOp",VERTEX,"E390.start");
            var Q5;
            Q5=sQuery(id+"F16.wireOp",VERTEX,"E398.MirrorCS.start");
            var Q6;
            Q6=sQuery(id+"F16.wireOp",VERTEX,"E398.MirrorCS.end");
            var Q7;
            Q7=sQuery(id+"F16.wireOp",VERTEX,"E392.MirrorCS.end");
            var Q8;
            Q8=sQuery(id+"F16.wireOp",VERTEX,"E394.MirrorCS.end");
            var Q9;
            Q9=sQuery(id+"F16.wireOp",VERTEX,"E394.MirrorCS.start");
            var Q10;
            Q10=makeQuery(id+"F1.opExtrude","SWEPT_BODY",BODY,{"disambiguationData":[OSD([sQuery(id+"F0.wireOp",EDGE,"E0.left"),sQuery(id+"F0.wireOp",EDGE,"E1.0"),sQuery(id+"F0.wireOp",EDGE,"E3.MirrorCS"),sQuery(id+"F0.wireOp",EDGE,"E5.MirrorCS")])]});
            var Q11;
            Q11=makeQuery(id+"F1.opExtrude","SWEPT_BODY",BODY,{"disambiguationData":[OSD([sQuery(id+"F0.wireOp",EDGE,"E0.right"),sQuery(id+"F0.wireOp",EDGE,"E1.2"),sQuery(id+"F0.wireOp",EDGE,"E2"),sQuery(id+"F0.wireOp",EDGE,"E4.MirrorCS")])]});
            var Q12;
            Q12=makeQuery(id+"F3.opExtrude","SWEPT_BODY",BODY,{"disambiguationData":[OSD([sQuery(id+"F0.wireOp",EDGE,"E1.0"),sQuery(id+"F0.wireOp",EDGE,"E1.1"),sQuery(id+"F0.wireOp",EDGE,"E19.MirrorCS"),sQuery(id+"F0.wireOp",EDGE,"E20.MirrorCS"),sQuery(id+"F0.wireOp",EDGE,"E21.MirrorCS"),sQuery(id+"F0.wireOp",EDGE,"E22.MirrorCS")])]});
            var Q13;
            Q13=makeQuery(id+"F3.opExtrude","SWEPT_BODY",BODY,{"disambiguationData":[OSD([sQuery(id+"F0.wireOp",EDGE,"E1.0"),sQuery(id+"F0.wireOp",EDGE,"E1.3"),sQuery(id+"F0.wireOp",EDGE,"E11.MirrorCS"),sQuery(id+"F0.wireOp",EDGE,"E12.MirrorCS"),sQuery(id+"F0.wireOp",EDGE,"E13.MirrorCS"),sQuery(id+"F0.wireOp",EDGE,"E14.MirrorCS")])]});
            var Q14;
            Q14=makeQuery(id+"F3.opExtrude","SWEPT_BODY",BODY,{"disambiguationData":[OSD([sQuery(id+"F0.wireOp",EDGE,"E1.1"),sQuery(id+"F0.wireOp",EDGE,"E1.2"),sQuery(id+"F0.wireOp",EDGE,"E15.MirrorCS"),sQuery(id+"F0.wireOp",EDGE,"E16.MirrorCS"),sQuery(id+"F0.wireOp",EDGE,"E17.MirrorCS"),sQuery(id+"F0.wireOp",EDGE,"E18.MirrorCS")])]});
            var Q15;
            Q15=makeQuery(id+"F3.opExtrude","SWEPT_BODY",BODY,{"disambiguationData":[OSD([sQuery(id+"F0.wireOp",EDGE,"E1.2"),sQuery(id+"F0.wireOp",EDGE,"E1.3"),sQuery(id+"F0.wireOp",EDGE,"E7"),sQuery(id+"F0.wireOp",EDGE,"E8"),sQuery(id+"F0.wireOp",EDGE,"E9"),sQuery(id+"F0.wireOp",EDGE,"E10")])]});
            hole(context, id + "F17", {"style" : HoleStyle.SIMPLE, "endStyle" : HoleEndStyle.THROUGH, "standardTappedOrClearance" : lookupTablePath({ "standard" : "ANSI", "fit" : "Close", "size" : "#4", "type" : "Clearance" }), "standardBlindInLast" : lookupTablePath({ "fit" : "Close", "standard" : "ANSI", "size" : "#4", "type" : "Clearance" }), "holeDiameter" : 2.95 * mm, "majorDiameter" : 6.35 * mm, "isTappedThrough" : true, "tappedDepth" : 12.7 * mm, "tapClearance" : 3, "locations" : qUnion([Q0, Q1, Q2, Q3, Q4, Q5, Q6, Q7, Q8, Q9]), "scope" : qUnion([Q10, Q11, Q12, Q13, Q14, Q15])});
        }
        {
            var Q0;
            Q0=makeQuery(id+"F5.opExtrude","SWEPT_FACE",FACE,{"disambiguationData":[OSD([sQuery(id+"F4.wireOp",EDGE,"E25")])]});
            var sketch = newSketch(context, id + "F18", { "sketchPlane" : qUnion([Q0])});
            skLineSegment(sketch, "E399", {"start": v(-219.08, -3.18) * mm, "end": v(-219.08, 9.52) * mm});
            skLineSegment(sketch, "E400", {"start": v(-219.08, 9.52) * mm, "end": v(219.07, 9.52) * mm});
            skLineSegment(sketch, "E401", {"start": v(0, 9.52) * mm, "end": v(0, -26.44) * mm});
            skLineSegment(sketch, "E402", {"start": v(0, 9.52) * mm, "end": v(-50.8, 9.52) * mm});
            skLineSegment(sketch, "E403", {"start": v(-50.8, 9.52) * mm, "end": v(-101.6, 9.52) * mm});
            skLineSegment(sketch, "E404", {"start": v(-101.6, 9.52) * mm, "end": v(-152.4, 9.52) * mm});
            skLineSegment(sketch, "E405", {"start": v(-152.4, 9.52) * mm, "end": v(-203.2, 9.52) * mm});
            skLineSegment(sketch, "E406.MirrorCS", {"start": v(152.4, 9.53) * mm, "end": v(203.2, 9.53) * mm});
            skLineSegment(sketch, "E407.MirrorCS", {"start": v(219.07, -3.17) * mm, "end": v(219.07, 9.53) * mm});
            skLineSegment(sketch, "E408.MirrorCS", {"start": v(0, 9.52) * mm, "end": v(50.8, 9.52) * mm});
            skLineSegment(sketch, "E409.MirrorCS", {"start": v(50.8, 9.52) * mm, "end": v(101.6, 9.52) * mm});
            skLineSegment(sketch, "E410.MirrorCS", {"start": v(101.6, 9.52) * mm, "end": v(152.4, 9.53) * mm});
            skSolve(sketch);
        }
        {
            var Q0;
            Q0=sQuery(id+"F18.wireOp",VERTEX,"E406.MirrorCS.end");
            var Q1;
            Q1=sQuery(id+"F18.wireOp",VERTEX,"E410.MirrorCS.end");
            var Q2;
            Q2=sQuery(id+"F18.wireOp",VERTEX,"E409.MirrorCS.end");
            var Q3;
            Q3=sQuery(id+"F18.wireOp",VERTEX,"E409.MirrorCS.start");
            var Q4;
            Q4=sQuery(id+"F18.wireOp",VERTEX,"E402.start");
            var Q5;
            Q5=sQuery(id+"F18.wireOp",VERTEX,"E402.start");
            var Q6;
            Q6=sQuery(id+"F18.wireOp",VERTEX,"E403.start");
            var Q7;
            Q7=sQuery(id+"F18.wireOp",VERTEX,"E403.start");
            var Q8;
            Q8=sQuery(id+"F18.wireOp",VERTEX,"E405.start");
            var Q9;
            Q9=sQuery(id+"F18.wireOp",VERTEX,"E403.end");
            var Q10;
            Q10=sQuery(id+"F18.wireOp",VERTEX,"E405.end");
            var Q11;
            Q11=makeQuery(id+"F5.opExtrude","SWEPT_BODY",BODY,{"disambiguationData":[OSD([sQuery(id+"F4.wireOp",EDGE,"E25"),sQuery(id+"F4.wireOp",EDGE,"E26"),sQuery(id+"F4.wireOp",EDGE,"E27"),sQuery(id+"F4.wireOp",EDGE,"E28"),sQuery(id+"F4.wireOp",EDGE,"E29"),sQuery(id+"F4.wireOp",EDGE,"E30")])]});
            var Q12;
            Q12=makeQuery(id+"F2.opExtrude","SWEPT_BODY",BODY,{"disambiguationData":[OSD([sQuery(id+"F0.wireOp",EDGE,"E0.bottom"),sQuery(id+"F0.wireOp",EDGE,"E1.0"),sQuery(id+"F0.wireOp",EDGE,"E1.1"),sQuery(id+"F0.wireOp",EDGE,"E1.2"),sQuery(id+"F0.wireOp",EDGE,"E4.MirrorCS"),sQuery(id+"F0.wireOp",EDGE,"E5.MirrorCS")])]});
            var Q13;
            Q13=makeQuery(id+"F2.opExtrude","SWEPT_BODY",BODY,{"disambiguationData":[OSD([sQuery(id+"F0.wireOp",EDGE,"E0.top"),sQuery(id+"F0.wireOp",EDGE,"E1.0"),sQuery(id+"F0.wireOp",EDGE,"E1.2"),sQuery(id+"F0.wireOp",EDGE,"E1.3"),sQuery(id+"F0.wireOp",EDGE,"E2"),sQuery(id+"F0.wireOp",EDGE,"E3.MirrorCS")])]});
            var Q14;
            Q14=makeQuery(id+"F7.opPattern","COPY",BODY,{"derivedFrom":makeQuery(id+"F5.opExtrude","SWEPT_BODY",BODY,{"disambiguationData":[OSD([sQuery(id+"F4.wireOp",EDGE,"E25"),sQuery(id+"F4.wireOp",EDGE,"E26"),sQuery(id+"F4.wireOp",EDGE,"E27"),sQuery(id+"F4.wireOp",EDGE,"E28"),sQuery(id+"F4.wireOp",EDGE,"E29"),sQuery(id+"F4.wireOp",EDGE,"E30")])]}),"instanceName":"2"});
            hole(context, id + "F19", {"style" : HoleStyle.SIMPLE, "endStyle" : HoleEndStyle.THROUGH, "standardTappedOrClearance" : lookupTablePath({ "standard" : "ANSI", "fit" : "Close", "size" : "#4", "type" : "Clearance" }), "standardBlindInLast" : lookupTablePath({ "fit" : "Close", "standard" : "ANSI", "size" : "#4", "type" : "Clearance" }), "holeDiameter" : 2.95 * mm, "majorDiameter" : 6.35 * mm, "isTappedThrough" : true, "tappedDepth" : 12.7 * mm, "tapClearance" : 3, "locations" : qUnion([Q0, Q1, Q2, Q3, Q4, Q5, Q6, Q7, Q8, Q9, Q10]), "scope" : qUnion([Q11, Q12, Q13, Q14])});
        }
        {
            var Q0;
            Q0=makeQuery(id+"F7.opPattern","COPY",FACE,{"derivedFrom":makeQuery(id+"F5.opExtrude","SWEPT_FACE",FACE,{"disambiguationData":[OSD([sQuery(id+"F4.wireOp",EDGE,"E25")])]}),"instanceName":"3"});
            var sketch = newSketch(context, id + "F20", { "sketchPlane" : qUnion([Q0])});
            skLineSegment(sketch, "E411", {"start": v(-219.08, 9.52) * mm, "end": v(-219.08, -3.18) * mm});
            skLineSegment(sketch, "E412", {"start": v(-219.08, 9.52) * mm, "end": v(219.08, 9.52) * mm});
            skLineSegment(sketch, "E413", {"start": v(0, 9.52) * mm, "end": v(0, -21.26) * mm});
            skPoint(sketch, "E413.endSnap0", {"position": v(0, 9.52) * mm});
            skLineSegment(sketch, "E414", {"start": v(0, 9.52) * mm, "end": v(-50.8, 9.52) * mm});
            skLineSegment(sketch, "E415", {"start": v(-50.8, 9.52) * mm, "end": v(-101.6, 9.52) * mm});
            skLineSegment(sketch, "E416", {"start": v(-101.6, 9.52) * mm, "end": v(-152.4, 9.52) * mm});
            skLineSegment(sketch, "E417", {"start": v(-152.4, 9.52) * mm, "end": v(-203.2, 9.52) * mm});
            skLineSegment(sketch, "E418.MirrorCS", {"start": v(152.4, 9.52) * mm, "end": v(203.2, 9.52) * mm});
            skLineSegment(sketch, "E419.MirrorCS", {"start": v(0, 9.52) * mm, "end": v(50.8, 9.52) * mm});
            skLineSegment(sketch, "E420.MirrorCS", {"start": v(219.08, 9.52) * mm, "end": v(219.08, -3.18) * mm});
            skLineSegment(sketch, "E421.MirrorCS", {"start": v(50.8, 9.52) * mm, "end": v(101.6, 9.52) * mm});
            skLineSegment(sketch, "E422.MirrorCS", {"start": v(101.6, 9.52) * mm, "end": v(152.4, 9.52) * mm});
            skSolve(sketch);
        }
        {
            var Q0;
            Q0=sQuery(id+"F20.wireOp",VERTEX,"E418.MirrorCS.end");
            var Q1;
            Q1=sQuery(id+"F20.wireOp",VERTEX,"E418.MirrorCS.start");
            var Q2;
            Q2=sQuery(id+"F20.wireOp",VERTEX,"E422.MirrorCS.start");
            var Q3;
            Q3=sQuery(id+"F20.wireOp",VERTEX,"E419.MirrorCS.end");
            var Q4;
            Q4=sQuery(id+"F20.wireOp",VERTEX,"E414.start");
            var Q5;
            Q5=sQuery(id+"F20.wireOp",VERTEX,"E415.start");
            var Q6;
            Q6=sQuery(id+"F20.wireOp",VERTEX,"E416.start");
            var Q7;
            Q7=sQuery(id+"F20.wireOp",VERTEX,"E416.end");
            var Q8;
            Q8=sQuery(id+"F20.wireOp",VERTEX,"E417.end");
            var Q9;
            Q9=makeQuery(id+"F1.opExtrude","SWEPT_BODY",BODY,{"disambiguationData":[OSD([sQuery(id+"F0.wireOp",EDGE,"E0.left"),sQuery(id+"F0.wireOp",EDGE,"E1.0"),sQuery(id+"F0.wireOp",EDGE,"E3.MirrorCS"),sQuery(id+"F0.wireOp",EDGE,"E5.MirrorCS")])]});
            var Q10;
            Q10=makeQuery(id+"F1.opExtrude","SWEPT_BODY",BODY,{"disambiguationData":[OSD([sQuery(id+"F0.wireOp",EDGE,"E0.right"),sQuery(id+"F0.wireOp",EDGE,"E1.2"),sQuery(id+"F0.wireOp",EDGE,"E2"),sQuery(id+"F0.wireOp",EDGE,"E4.MirrorCS")])]});
            var Q11;
            Q11=makeQuery(id+"F7.opPattern","COPY",BODY,{"derivedFrom":makeQuery(id+"F5.opExtrude","SWEPT_BODY",BODY,{"disambiguationData":[OSD([sQuery(id+"F4.wireOp",EDGE,"E25"),sQuery(id+"F4.wireOp",EDGE,"E26"),sQuery(id+"F4.wireOp",EDGE,"E27"),sQuery(id+"F4.wireOp",EDGE,"E28"),sQuery(id+"F4.wireOp",EDGE,"E29"),sQuery(id+"F4.wireOp",EDGE,"E30")])]}),"instanceName":"1"});
            var Q12;
            Q12=makeQuery(id+"F7.opPattern","COPY",BODY,{"derivedFrom":makeQuery(id+"F5.opExtrude","SWEPT_BODY",BODY,{"disambiguationData":[OSD([sQuery(id+"F4.wireOp",EDGE,"E25"),sQuery(id+"F4.wireOp",EDGE,"E26"),sQuery(id+"F4.wireOp",EDGE,"E27"),sQuery(id+"F4.wireOp",EDGE,"E28"),sQuery(id+"F4.wireOp",EDGE,"E29"),sQuery(id+"F4.wireOp",EDGE,"E30")])]}),"instanceName":"3"});
            hole(context, id + "F21", {"style" : HoleStyle.SIMPLE, "endStyle" : HoleEndStyle.THROUGH, "standardTappedOrClearance" : lookupTablePath({ "standard" : "ANSI", "fit" : "Close", "size" : "#4", "type" : "Clearance" }), "standardBlindInLast" : lookupTablePath({ "fit" : "Close", "standard" : "ANSI", "size" : "#4", "type" : "Clearance" }), "holeDiameter" : 2.95 * mm, "majorDiameter" : 6.35 * mm, "isTappedThrough" : true, "tappedDepth" : 12.7 * mm, "tapClearance" : 3, "locations" : qUnion([Q0, Q1, Q2, Q3, Q4, Q5, Q6, Q7, Q8]), "scope" : qUnion([Q9, Q10, Q11, Q12])});
        }
        {
            var Q0;
            Q0=makeQuery(id+"F7.opPattern","COPY",FACE,{"derivedFrom":makeQuery(id+"F5.opExtrude","SWEPT_FACE",FACE,{"disambiguationData":[OSD([sQuery(id+"F4.wireOp",EDGE,"E28")])]}),"instanceName":"3"});
            var sketch = newSketch(context, id + "F22", { "sketchPlane" : qUnion([Q0])});
            skLineSegment(sketch, "E423", {"start": v(-238.13, 219.07) * mm, "end": v(-225.43, 219.07) * mm});
            skLineSegment(sketch, "E424", {"start": v(-225.43, 219.07) * mm, "end": v(-225.43, -219.08) * mm});
            skLineSegment(sketch, "E425", {"start": v(-225.43, 0) * mm, "end": v(-273.05, 0) * mm});
            skLineSegment(sketch, "E426", {"start": v(-225.43, 0) * mm, "end": v(-225.43, 25.4) * mm});
            skLineSegment(sketch, "E427", {"start": v(-225.43, 25.4) * mm, "end": v(-225.43, 76.2) * mm});
            skLineSegment(sketch, "E428", {"start": v(-225.43, 76.2) * mm, "end": v(-225.43, 127) * mm});
            skLineSegment(sketch, "E429", {"start": v(-225.43, 127) * mm, "end": v(-225.43, 177.8) * mm});
            skLineSegment(sketch, "E430.MirrorCS", {"start": v(-238.13, -219.08) * mm, "end": v(-225.43, -219.08) * mm});
            skLineSegment(sketch, "E431.MirrorCS", {"start": v(-225.43, 0) * mm, "end": v(-225.43, -25.4) * mm});
            skLineSegment(sketch, "E432.MirrorCS", {"start": v(-225.43, -127) * mm, "end": v(-225.43, -177.8) * mm});
            skLineSegment(sketch, "E433.MirrorCS", {"start": v(-225.43, -25.4) * mm, "end": v(-225.43, -76.2) * mm});
            skLineSegment(sketch, "E434.MirrorCS", {"start": v(-225.43, -76.2) * mm, "end": v(-225.43, -127) * mm});
            skLineSegment(sketch, "E435.1.0", {"start": v(0, -225.43) * mm, "end": v(-25.4, -225.43) * mm});
            skLineSegment(sketch, "E435.1.1", {"start": v(-219.07, -238.13) * mm, "end": v(-219.07, -225.43) * mm});
            skLineSegment(sketch, "E435.1.2", {"start": v(0, -225.43) * mm, "end": v(0, -273.05) * mm});
            skLineSegment(sketch, "E435.1.3", {"start": v(219.08, -238.13) * mm, "end": v(219.08, -225.43) * mm});
            skLineSegment(sketch, "E435.1.4", {"start": v(127, -225.43) * mm, "end": v(177.8, -225.43) * mm});
            skLineSegment(sketch, "E435.1.5", {"start": v(-25.4, -225.43) * mm, "end": v(-76.2, -225.43) * mm});
            skLineSegment(sketch, "E435.1.6", {"start": v(0, -225.43) * mm, "end": v(0, -273.05) * mm});
            skLineSegment(sketch, "E435.1.7", {"start": v(0, -225.43) * mm, "end": v(25.4, -225.43) * mm});
            skLineSegment(sketch, "E435.1.8", {"start": v(25.4, -225.43) * mm, "end": v(76.2, -225.43) * mm});
            skLineSegment(sketch, "E435.1.9", {"start": v(76.2, -225.43) * mm, "end": v(127, -225.43) * mm});
            skLineSegment(sketch, "E435.1.10", {"start": v(-127, -225.43) * mm, "end": v(-177.8, -225.43) * mm});
            skLineSegment(sketch, "E435.1.11", {"start": v(-76.2, -225.43) * mm, "end": v(-127, -225.43) * mm});
            skLineSegment(sketch, "E435.1.12", {"start": v(-219.07, -225.43) * mm, "end": v(219.08, -225.43) * mm});
            skLineSegment(sketch, "E435.2.0", {"start": v(225.43, 0) * mm, "end": v(225.43, -25.4) * mm});
            skLineSegment(sketch, "E435.2.1", {"start": v(238.12, -219.07) * mm, "end": v(225.43, -219.07) * mm});
            skLineSegment(sketch, "E435.2.2", {"start": v(225.43, 0) * mm, "end": v(273.05, 0) * mm});
            skLineSegment(sketch, "E435.2.3", {"start": v(238.13, 219.08) * mm, "end": v(225.43, 219.08) * mm});
            skLineSegment(sketch, "E435.2.4", {"start": v(225.43, 127) * mm, "end": v(225.43, 177.8) * mm});
            skLineSegment(sketch, "E435.2.5", {"start": v(225.43, -25.4) * mm, "end": v(225.43, -76.2) * mm});
            skLineSegment(sketch, "E435.2.6", {"start": v(225.43, 0) * mm, "end": v(273.05, 0) * mm});
            skLineSegment(sketch, "E435.2.7", {"start": v(225.43, 0) * mm, "end": v(225.43, 25.4) * mm});
            skLineSegment(sketch, "E435.2.8", {"start": v(225.43, 25.4) * mm, "end": v(225.43, 76.2) * mm});
            skLineSegment(sketch, "E435.2.9", {"start": v(225.43, 76.2) * mm, "end": v(225.43, 127) * mm});
            skLineSegment(sketch, "E435.2.10", {"start": v(225.43, -127) * mm, "end": v(225.43, -177.8) * mm});
            skLineSegment(sketch, "E435.2.11", {"start": v(225.43, -76.2) * mm, "end": v(225.43, -127) * mm});
            skLineSegment(sketch, "E435.2.12", {"start": v(225.43, -219.07) * mm, "end": v(225.43, 219.08) * mm});
            skLineSegment(sketch, "E435.3.0", {"start": v(0, 225.43) * mm, "end": v(25.4, 225.43) * mm});
            skLineSegment(sketch, "E435.3.1", {"start": v(219.08, 238.12) * mm, "end": v(219.08, 225.43) * mm});
            skLineSegment(sketch, "E435.3.2", {"start": v(0, 225.43) * mm, "end": v(0, 273.05) * mm});
            skLineSegment(sketch, "E435.3.3", {"start": v(-219.08, 238.13) * mm, "end": v(-219.08, 225.43) * mm});
            skLineSegment(sketch, "E435.3.4", {"start": v(-127, 225.43) * mm, "end": v(-177.8, 225.43) * mm});
            skLineSegment(sketch, "E435.3.5", {"start": v(25.4, 225.43) * mm, "end": v(76.2, 225.43) * mm});
            skLineSegment(sketch, "E435.3.6", {"start": v(0, 225.43) * mm, "end": v(0, 273.05) * mm});
            skLineSegment(sketch, "E435.3.7", {"start": v(0, 225.43) * mm, "end": v(-25.4, 225.43) * mm});
            skLineSegment(sketch, "E435.3.8", {"start": v(-25.4, 225.43) * mm, "end": v(-76.2, 225.43) * mm});
            skLineSegment(sketch, "E435.3.9", {"start": v(-76.2, 225.43) * mm, "end": v(-127, 225.43) * mm});
            skLineSegment(sketch, "E435.3.10", {"start": v(127, 225.43) * mm, "end": v(177.8, 225.43) * mm});
            skLineSegment(sketch, "E435.3.11", {"start": v(76.2, 225.43) * mm, "end": v(127, 225.43) * mm});
            skLineSegment(sketch, "E435.3.12", {"start": v(219.07, 225.43) * mm, "end": v(-219.08, 225.43) * mm});
            skPoint(sketch, "E435.center", {"position": v(0, 0) * mm});
            skSolve(sketch);
        }
        {
            var Q0;
            Q0=sQuery(id+"F22.wireOp",VERTEX,"E432.MirrorCS.end");
            var Q1;
            Q1=sQuery(id+"F22.wireOp",VERTEX,"E434.MirrorCS.end");
            var Q2;
            Q2=sQuery(id+"F22.wireOp",VERTEX,"E434.MirrorCS.start");
            var Q3;
            Q3=sQuery(id+"F22.wireOp",VERTEX,"E431.MirrorCS.end");
            var Q4;
            Q4=sQuery(id+"F22.wireOp",VERTEX,"E426.end");
            var Q5;
            Q5=sQuery(id+"F22.wireOp",VERTEX,"E427.end");
            var Q6;
            Q6=sQuery(id+"F22.wireOp",VERTEX,"E429.start");
            var Q7;
            Q7=sQuery(id+"F22.wireOp",VERTEX,"E429.end");
            var Q8;
            Q8=sQuery(id+"F22.wireOp",VERTEX,"E435.3.4.end");
            var Q9;
            Q9=sQuery(id+"F22.wireOp",VERTEX,"E435.3.9.end");
            var Q10;
            Q10=sQuery(id+"F22.wireOp",VERTEX,"E435.3.7.end");
            var Q11;
            Q11=sQuery(id+"F22.wireOp",VERTEX,"E435.3.8.end");
            var Q12;
            Q12=sQuery(id+"F22.wireOp",VERTEX,"E435.2.9.start");
            var Q13;
            Q13=sQuery(id+"F22.wireOp",VERTEX,"E435.2.7.end");
            var Q14;
            Q14=sQuery(id+"F22.wireOp",VERTEX,"E435.3.11.start");
            var Q15;
            Q15=sQuery(id+"F22.wireOp",VERTEX,"E435.3.5.start");
            var Q16;
            Q16=sQuery(id+"F22.wireOp",VERTEX,"E435.3.10.start");
            var Q17;
            Q17=sQuery(id+"F22.wireOp",VERTEX,"E435.3.10.end");
            var Q18;
            Q18=sQuery(id+"F22.wireOp",VERTEX,"E435.2.4.start");
            var Q19;
            Q19=sQuery(id+"F22.wireOp",VERTEX,"E435.2.4.end");
            var Q20;
            Q20=makeQuery(id+"F5.opExtrude","SWEPT_BODY",BODY,{"disambiguationData":[OSD([sQuery(id+"F4.wireOp",EDGE,"E25"),sQuery(id+"F4.wireOp",EDGE,"E26"),sQuery(id+"F4.wireOp",EDGE,"E27"),sQuery(id+"F4.wireOp",EDGE,"E28"),sQuery(id+"F4.wireOp",EDGE,"E29"),sQuery(id+"F4.wireOp",EDGE,"E30")])]});
            var Q21;
            Q21=makeQuery(id+"F7.opPattern","COPY",BODY,{"derivedFrom":makeQuery(id+"F5.opExtrude","SWEPT_BODY",BODY,{"disambiguationData":[OSD([sQuery(id+"F4.wireOp",EDGE,"E25"),sQuery(id+"F4.wireOp",EDGE,"E26"),sQuery(id+"F4.wireOp",EDGE,"E27"),sQuery(id+"F4.wireOp",EDGE,"E28"),sQuery(id+"F4.wireOp",EDGE,"E29"),sQuery(id+"F4.wireOp",EDGE,"E30")])]}),"instanceName":"3"});
            var Q22;
            Q22=makeQuery(id+"F13.opExtrude","SWEPT_BODY",BODY,{"disambiguationData":[OSD([sQuery(id+"F12.wireOp",EDGE,"E273.bottom"),sQuery(id+"F12.wireOp",EDGE,"E273.top"),sQuery(id+"F12.wireOp",EDGE,"E273.left"),sQuery(id+"F12.wireOp",EDGE,"E273.right"),sQuery(id+"F12.wireOp",EDGE,"E275.0"),sQuery(id+"F12.wireOp",EDGE,"E275.1"),sQuery(id+"F12.wireOp",EDGE,"E275.2"),sQuery(id+"F12.wireOp",EDGE,"E275.3"),sQuery(id+"F12.wireOp",EDGE,"E276.filletArc"),sQuery(id+"F12.wireOp",EDGE,"E277.filletArc"),sQuery(id+"F12.wireOp",EDGE,"E278.filletArc"),sQuery(id+"F12.wireOp",EDGE,"E279.filletArc"),sQuery(id+"F12.wireOp",EDGE,"E280.MirrorCS"),sQuery(id+"F12.wireOp",EDGE,"E281.MirrorCS"),sQuery(id+"F12.wireOp",EDGE,"E282.MirrorCS"),sQuery(id+"F12.wireOp",EDGE,"E284.MirrorCS"),sQuery(id+"F12.wireOp",EDGE,"E287.MirrorCS"),sQuery(id+"F12.wireOp",EDGE,"E288.MirrorCS"),sQuery(id+"F12.wireOp",EDGE,"E289.MirrorCS"),sQuery(id+"F12.wireOp",EDGE,"E291.MirrorCS"),sQuery(id+"F12.wireOp",EDGE,"E292.MirrorCS"),sQuery(id+"F12.wireOp",EDGE,"E295.MirrorCS"),sQuery(id+"F12.wireOp",EDGE,"E296.MirrorCS"),sQuery(id+"F12.wireOp",EDGE,"E297.MirrorCS"),sQuery(id+"F12.wireOp",EDGE,"E298.MirrorCS"),sQuery(id+"F12.wireOp",EDGE,"E299.MirrorCS"),sQuery(id+"F12.wireOp",EDGE,"E303.MirrorCS"),sQuery(id+"F12.wireOp",EDGE,"E304.MirrorCS"),sQuery(id+"F12.wireOp",EDGE,"E305.MirrorCS"),sQuery(id+"F12.wireOp",EDGE,"E306.MirrorCS"),sQuery(id+"F12.wireOp",EDGE,"E309.MirrorCS"),sQuery(id+"F12.wireOp",EDGE,"E310.MirrorCS"),sQuery(id+"F12.wireOp",EDGE,"E311.MirrorCS"),sQuery(id+"F12.wireOp",EDGE,"E313.MirrorCS"),sQuery(id+"F12.wireOp",EDGE,"E314.MirrorCS"),sQuery(id+"F12.wireOp",EDGE,"E315.MirrorCS"),sQuery(id+"F12.wireOp",EDGE,"E318.MirrorCS"),sQuery(id+"F12.wireOp",EDGE,"E319.MirrorCS"),sQuery(id+"F12.wireOp",EDGE,"E320.MirrorCS"),sQuery(id+"F12.wireOp",EDGE,"E322.MirrorCS"),sQuery(id+"F12.wireOp",EDGE,"E325.MirrorCS"),sQuery(id+"F12.wireOp",EDGE,"E326.MirrorCS"),sQuery(id+"F12.wireOp",EDGE,"E328.MirrorCS"),sQuery(id+"F12.wireOp",EDGE,"E329.MirrorCS"),sQuery(id+"F12.wireOp",EDGE,"E330.MirrorCS"),sQuery(id+"F12.wireOp",EDGE,"E332.MirrorCS"),sQuery(id+"F12.wireOp",EDGE,"E334.MirrorCS"),sQuery(id+"F12.wireOp",EDGE,"E336.MirrorCS"),sQuery(id+"F12.wireOp",EDGE,"E338.MirrorCS"),sQuery(id+"F12.wireOp",EDGE,"E339.MirrorCS"),sQuery(id+"F12.wireOp",EDGE,"E340.MirrorCS"),sQuery(id+"F12.wireOp",EDGE,"E341.MirrorCS"),sQuery(id+"F12.wireOp",EDGE,"E342.MirrorCS"),sQuery(id+"F12.wireOp",EDGE,"E343.MirrorCS"),sQuery(id+"F12.wireOp",EDGE,"E345.MirrorCS"),sQuery(id+"F12.wireOp",EDGE,"E346.MirrorCS"),sQuery(id+"F12.wireOp",EDGE,"E348.MirrorCS"),sQuery(id+"F12.wireOp",EDGE,"E349.MirrorCS"),sQuery(id+"F12.wireOp",EDGE,"E350.MirrorCS"),sQuery(id+"F12.wireOp",EDGE,"E352.MirrorCS"),sQuery(id+"F12.wireOp",EDGE,"E353.MirrorCS"),sQuery(id+"F12.wireOp",EDGE,"E355.MirrorCS"),sQuery(id+"F12.wireOp",EDGE,"E356.MirrorCS"),sQuery(id+"F12.wireOp",EDGE,"E357.MirrorCS"),sQuery(id+"F12.wireOp",EDGE,"E359.MirrorCS"),sQuery(id+"F12.wireOp",EDGE,"E360.MirrorCS"),sQuery(id+"F12.wireOp",EDGE,"E362.MirrorCS"),sQuery(id+"F12.wireOp",EDGE,"E363.MirrorCS")])]});
            hole(context, id + "F23", {"style" : HoleStyle.SIMPLE, "endStyle" : HoleEndStyle.THROUGH, "standardTappedOrClearance" : lookupTablePath({ "standard" : "ANSI", "fit" : "Close", "size" : "#4", "type" : "Clearance" }), "standardBlindInLast" : lookupTablePath({ "fit" : "Close", "standard" : "ANSI", "size" : "#4", "type" : "Clearance" }), "holeDiameter" : 2.95 * mm, "majorDiameter" : 6.35 * mm, "isTappedThrough" : true, "tappedDepth" : 12.7 * mm, "tapClearance" : 3, "locations" : qUnion([Q0, Q1, Q2, Q3, Q4, Q5, Q6, Q7, Q8, Q9, Q10, Q11, Q12, Q13, Q14, Q15, Q16, Q17, Q18, Q19]), "scope" : qUnion([Q20, Q21, Q22])});
        }
    });
